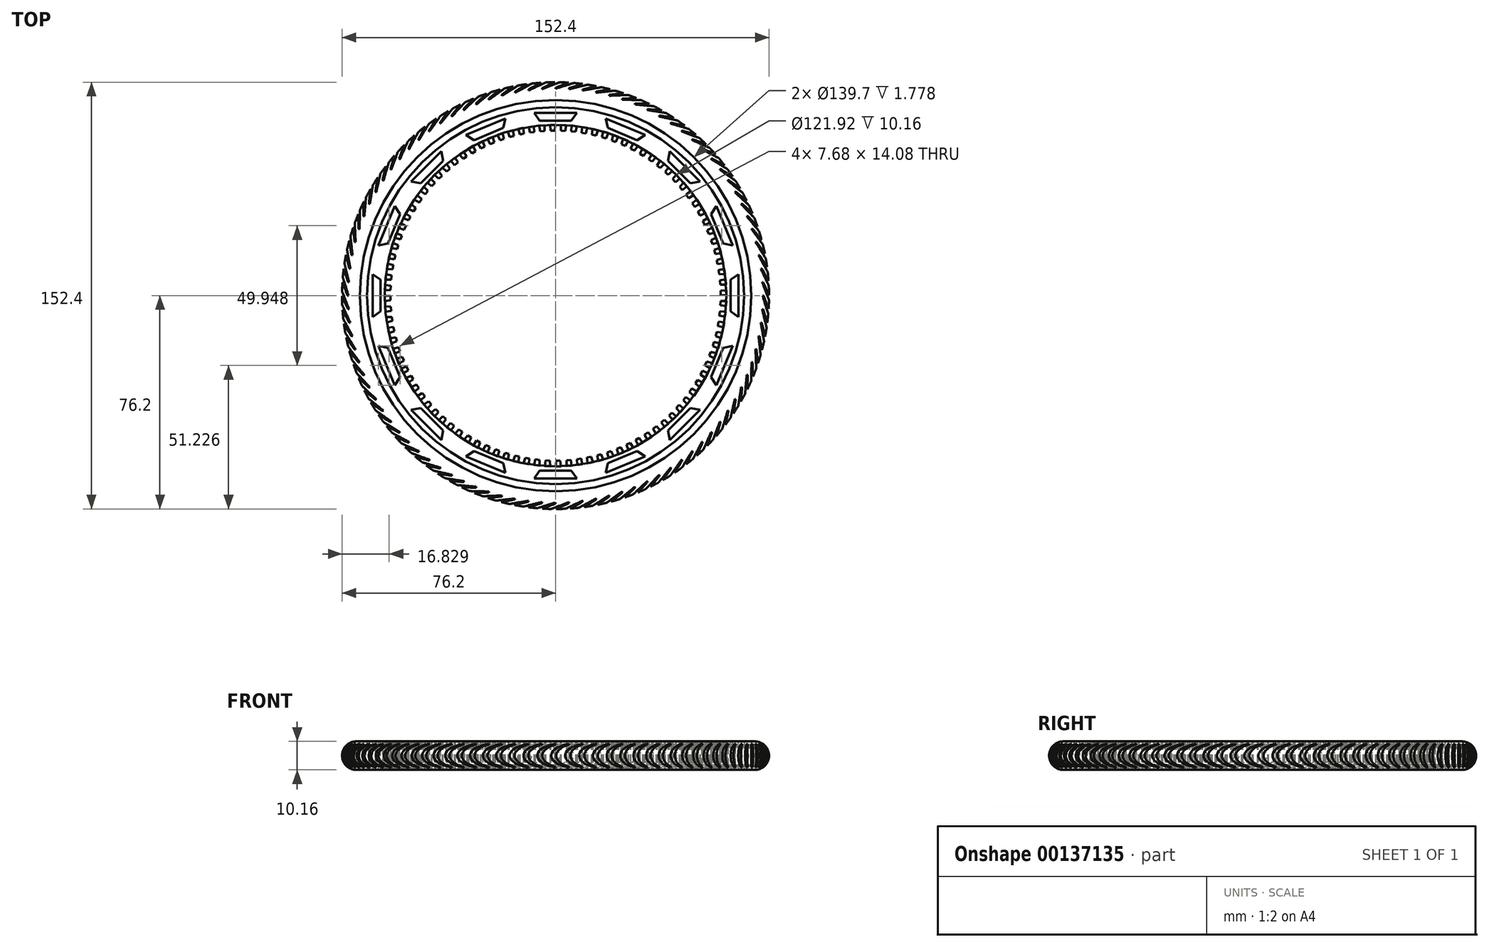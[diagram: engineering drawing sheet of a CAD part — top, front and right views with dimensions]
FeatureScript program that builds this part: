
annotation { "Feature Type Name" : "Feature", "Feature Type Description" : "" }
export const myFeature = defineFeature(function(context is Context, id is Id, definition is map)
    precondition{}
    {
        {
            var Q0;
            Q0=qCreatedBy(makeId("Top.planeOp"),FACE);
            var sketch = newSketch(context, id + "F0", { "sketchPlane" : qUnion([Q0])});
            skCircle(sketch, "E0", {"center": v(0, 0) * mm, "radius": 76.2 * mm});
            skCircle(sketch, "E1", {"center": v(0, 0) * mm, "radius": 60.96 * mm});
            skSolve(sketch);
        }
        {
            var Q0;
            Q0 = qSketchRegion(id + "F0", true);
            extrude(context, id + "F1", {"entities" : qUnion([Q0]), "depth" : 10.16 * mm});
        }
        {
            var Q0;
            Q0=makeQuery(id+"F1.opExtrude","SWEPT_FACE",FACE,{"disambiguationData":[OSD([sQuery(id+"F0.wireOp",EDGE,"E0")])]});
            fillet(context, id + "F2", {"entities" : qUnion([Q0]), "radius" : 5.08 * mm, "tangentPropagation" : true, "allowEdgeOverflow" : false});
        }
        {
            var Q0;
            Q0=qCreatedBy(makeId("Front.planeOp"),FACE);
            var sketch = newSketch(context, id + "F3", { "sketchPlane" : qUnion([Q0])});
            skLineSegment(sketch, "E2", {"start": v(0, 10.16) * mm, "end": v(-69.85, 10.16) * mm, "construction": true});
            skLineSegment(sketch, "E3", {"start": v(-69.85, 10.16) * mm, "end": v(-69.85, 0) * mm, "construction": true});
            skLineSegment(sketch, "E4.bottom", {"start": v(-69.85, 0) * mm, "end": v(-67.31, 0) * mm});
            skLineSegment(sketch, "E4.top", {"start": v(-69.85, 1.78) * mm, "end": v(-67.31, 1.78) * mm});
            skLineSegment(sketch, "E4.left", {"start": v(-69.85, 0) * mm, "end": v(-69.85, 1.78) * mm});
            skLineSegment(sketch, "E4.right", {"start": v(-67.31, 0) * mm, "end": v(-67.31, 1.78) * mm});
            skLineSegment(sketch, "E5.bottom", {"start": v(-69.85, 10.16) * mm, "end": v(-67.31, 10.16) * mm});
            skLineSegment(sketch, "E5.top", {"start": v(-69.85, 8.38) * mm, "end": v(-67.31, 8.38) * mm});
            skLineSegment(sketch, "E5.left", {"start": v(-69.85, 10.16) * mm, "end": v(-69.85, 8.38) * mm});
            skLineSegment(sketch, "E5.right", {"start": v(-67.31, 10.16) * mm, "end": v(-67.31, 8.38) * mm});
            skSolve(sketch);
        }
        {
            var Q0;
            Q0=qCreatedBy(makeId("Front.planeOp"),FACE);
            var sketch = newSketch(context, id + "F4", { "sketchPlane" : qUnion([Q0])});
            skLineSegment(sketch, "E6", {"start": v(0, 100.83) * mm, "end": v(0, -94.42) * mm, "construction": true});
            skSolve(sketch);
        }
        {
            var Q0;
            Q0 = qSketchRegion(id + "F3", true);
            var Q1;
            Q1=sQuery(id+"F4.wireOp",EDGE,"E6");
            revolve(context, id + "F5", {"operationType" : NewBodyOperationType.REMOVE, "entities" : qUnion([Q0]), "axis" : qUnion([Q1]), "revolveType" : RevolveType.FULL, "oppositeDirection" : true});
        }
        {
            var Q0;
            {var subQ0=sQuery(id+"F0.wireOp",EDGE,"E1");Q0=makeQuery(id+"F5.boolean.opBoolean","SPLIT",FACE,{"disambiguationData":[TD([makeQuery(id+"F1.opExtrude","SWEPT_FACE",FACE,{"disambiguationData":[OSD([subQ0])]})])],"derivedFrom":makeQuery(id+"F1.opExtrude","CAP_FACE",FACE,{"disambiguationData":[OSD([sQuery(id+"F0.wireOp",EDGE,"E0"),subQ0])],"isStart":true})});}
            var sketch = newSketch(context, id + "F6", { "sketchPlane" : qUnion([Q0])});
            skLineSegment(sketch, "E7", {"start": v(3.9, 60.84) * mm, "end": v(3.9, 58.8) * mm});
            skLineSegment(sketch, "E8", {"start": v(3.9, 58.8) * mm, "end": v(5.43, 58.68) * mm});
            skLineSegment(sketch, "E9", {"start": v(5.43, 58.68) * mm, "end": v(5.76, 60.69) * mm});
            skLineSegment(sketch, "E10", {"start": v(3.9, 60.84) * mm, "end": v(5.76, 60.69) * mm});
            skLineSegment(sketch, "E11.1.0", {"start": v(0.06, 60.96) * mm, "end": v(0.2, 58.93) * mm});
            skLineSegment(sketch, "E11.1.1", {"start": v(0.06, 60.96) * mm, "end": v(1.94, 60.93) * mm});
            skLineSegment(sketch, "E11.1.2", {"start": v(1.73, 58.9) * mm, "end": v(1.94, 60.93) * mm});
            skLineSegment(sketch, "E11.1.3", {"start": v(0.2, 58.93) * mm, "end": v(1.73, 58.9) * mm});
            skLineSegment(sketch, "E11.2.0", {"start": v(-3.76, 60.84) * mm, "end": v(-3.5, 58.83) * mm});
            skLineSegment(sketch, "E11.2.1", {"start": v(-3.76, 60.84) * mm, "end": v(-1.89, 60.93) * mm});
            skLineSegment(sketch, "E11.2.2", {"start": v(-1.97, 58.9) * mm, "end": v(-1.89, 60.93) * mm});
            skLineSegment(sketch, "E11.2.3", {"start": v(-3.5, 58.83) * mm, "end": v(-1.97, 58.9) * mm});
            skLineSegment(sketch, "E11.3.0", {"start": v(-7.58, 60.49) * mm, "end": v(-7.18, 58.5) * mm});
            skLineSegment(sketch, "E11.3.1", {"start": v(-7.58, 60.49) * mm, "end": v(-5.71, 60.7) * mm});
            skLineSegment(sketch, "E11.3.2", {"start": v(-5.67, 58.66) * mm, "end": v(-5.71, 60.7) * mm});
            skLineSegment(sketch, "E11.3.3", {"start": v(-7.18, 58.5) * mm, "end": v(-5.67, 58.66) * mm});
            skLineSegment(sketch, "E11.4.0", {"start": v(-11.36, 59.9) * mm, "end": v(-10.84, 57.93) * mm});
            skLineSegment(sketch, "E11.4.1", {"start": v(-11.36, 59.9) * mm, "end": v(-9.51, 60.21) * mm});
            skLineSegment(sketch, "E11.4.2", {"start": v(-9.34, 58.19) * mm, "end": v(-9.51, 60.21) * mm});
            skLineSegment(sketch, "E11.4.3", {"start": v(-10.84, 57.93) * mm, "end": v(-9.34, 58.19) * mm});
            skLineSegment(sketch, "E11.5.0", {"start": v(-15.1, 59.06) * mm, "end": v(-14.46, 57.13) * mm});
            skLineSegment(sketch, "E11.5.1", {"start": v(-15.1, 59.06) * mm, "end": v(-13.27, 59.5) * mm});
            skLineSegment(sketch, "E11.5.2", {"start": v(-12.97, 57.49) * mm, "end": v(-13.27, 59.5) * mm});
            skLineSegment(sketch, "E11.5.3", {"start": v(-14.46, 57.13) * mm, "end": v(-12.97, 57.49) * mm});
            skLineSegment(sketch, "E11.6.0", {"start": v(-18.78, 58) * mm, "end": v(-18.01, 56.11) * mm});
            skLineSegment(sketch, "E11.6.1", {"start": v(-18.78, 58) * mm, "end": v(-16.98, 58.55) * mm});
            skLineSegment(sketch, "E11.6.2", {"start": v(-16.56, 56.56) * mm, "end": v(-16.98, 58.55) * mm});
            skLineSegment(sketch, "E11.6.3", {"start": v(-18.01, 56.11) * mm, "end": v(-16.56, 56.56) * mm});
            skLineSegment(sketch, "E11.7.0", {"start": v(-22.38, 56.7) * mm, "end": v(-21.5, 54.87) * mm});
            skLineSegment(sketch, "E11.7.1", {"start": v(-22.38, 56.7) * mm, "end": v(-20.62, 57.37) * mm});
            skLineSegment(sketch, "E11.7.2", {"start": v(-20.08, 55.4) * mm, "end": v(-20.62, 57.37) * mm});
            skLineSegment(sketch, "E11.7.3", {"start": v(-21.5, 54.87) * mm, "end": v(-20.08, 55.4) * mm});
            skLineSegment(sketch, "E11.8.0", {"start": v(-25.9, 55.19) * mm, "end": v(-24.9, 53.41) * mm});
            skLineSegment(sketch, "E11.8.1", {"start": v(-25.9, 55.19) * mm, "end": v(-24.19, 55.96) * mm});
            skLineSegment(sketch, "E11.8.2", {"start": v(-23.52, 54.04) * mm, "end": v(-24.19, 55.96) * mm});
            skLineSegment(sketch, "E11.8.3", {"start": v(-24.9, 53.41) * mm, "end": v(-23.52, 54.04) * mm});
            skLineSegment(sketch, "E11.9.0", {"start": v(-29.31, 53.45) * mm, "end": v(-28.2, 51.74) * mm});
            skLineSegment(sketch, "E11.9.1", {"start": v(-29.31, 53.45) * mm, "end": v(-27.65, 54.33) * mm});
            skLineSegment(sketch, "E11.9.2", {"start": v(-26.86, 52.46) * mm, "end": v(-27.65, 54.33) * mm});
            skLineSegment(sketch, "E11.9.3", {"start": v(-28.2, 51.74) * mm, "end": v(-26.86, 52.46) * mm});
            skLineSegment(sketch, "E11.10.0", {"start": v(-32.61, 51.5) * mm, "end": v(-31.4, 49.87) * mm});
            skLineSegment(sketch, "E11.10.1", {"start": v(-32.61, 51.5) * mm, "end": v(-31, 52.48) * mm});
            skLineSegment(sketch, "E11.10.2", {"start": v(-30.1, 50.67) * mm, "end": v(-31, 52.48) * mm});
            skLineSegment(sketch, "E11.10.3", {"start": v(-31.4, 49.87) * mm, "end": v(-30.1, 50.67) * mm});
            skLineSegment(sketch, "E11.11.0", {"start": v(-35.78, 49.35) * mm, "end": v(-34.47, 47.8) * mm});
            skLineSegment(sketch, "E11.11.1", {"start": v(-35.78, 49.35) * mm, "end": v(-34.24, 50.43) * mm});
            skLineSegment(sketch, "E11.11.2", {"start": v(-33.23, 48.67) * mm, "end": v(-34.24, 50.43) * mm});
            skLineSegment(sketch, "E11.11.3", {"start": v(-34.47, 47.8) * mm, "end": v(-33.23, 48.67) * mm});
            skLineSegment(sketch, "E11.12.0", {"start": v(-38.8, 47.01) * mm, "end": v(-37.4, 45.54) * mm});
            skLineSegment(sketch, "E11.12.1", {"start": v(-38.8, 47.01) * mm, "end": v(-37.34, 48.18) * mm});
            skLineSegment(sketch, "E11.12.2", {"start": v(-36.22, 46.5) * mm, "end": v(-37.34, 48.18) * mm});
            skLineSegment(sketch, "E11.12.3", {"start": v(-37.4, 45.54) * mm, "end": v(-36.22, 46.5) * mm});
            skLineSegment(sketch, "E11.13.0", {"start": v(-41.68, 44.48) * mm, "end": v(-40.2, 43.1) * mm});
            skLineSegment(sketch, "E11.13.1", {"start": v(-41.68, 44.48) * mm, "end": v(-40.3, 45.74) * mm});
            skLineSegment(sketch, "E11.13.2", {"start": v(-39.06, 44.13) * mm, "end": v(-40.3, 45.74) * mm});
            skLineSegment(sketch, "E11.13.3", {"start": v(-40.2, 43.1) * mm, "end": v(-39.06, 44.13) * mm});
            skLineSegment(sketch, "E11.14.0", {"start": v(-44.4, 41.78) * mm, "end": v(-42.82, 40.5) * mm});
            skLineSegment(sketch, "E11.14.1", {"start": v(-44.4, 41.78) * mm, "end": v(-43.09, 43.12) * mm});
            skLineSegment(sketch, "E11.14.2", {"start": v(-41.76, 41.59) * mm, "end": v(-43.09, 43.12) * mm});
            skLineSegment(sketch, "E11.14.3", {"start": v(-42.82, 40.5) * mm, "end": v(-41.76, 41.59) * mm});
            skLineSegment(sketch, "E11.15.0", {"start": v(-46.93, 38.9) * mm, "end": v(-45.28, 37.72) * mm});
            skLineSegment(sketch, "E11.15.1", {"start": v(-46.93, 38.9) * mm, "end": v(-45.7, 40.33) * mm});
            skLineSegment(sketch, "E11.15.2", {"start": v(-44.29, 38.88) * mm, "end": v(-45.7, 40.33) * mm});
            skLineSegment(sketch, "E11.15.3", {"start": v(-45.28, 37.72) * mm, "end": v(-44.29, 38.88) * mm});
            skLineSegment(sketch, "E11.16.0", {"start": v(-49.28, 35.88) * mm, "end": v(-47.56, 34.8) * mm});
            skLineSegment(sketch, "E11.16.1", {"start": v(-49.28, 35.88) * mm, "end": v(-48.15, 37.38) * mm});
            skLineSegment(sketch, "E11.16.2", {"start": v(-46.64, 36.03) * mm, "end": v(-48.15, 37.38) * mm});
            skLineSegment(sketch, "E11.16.3", {"start": v(-47.56, 34.8) * mm, "end": v(-46.64, 36.03) * mm});
            skLineSegment(sketch, "E11.17.0", {"start": v(-51.44, 32.72) * mm, "end": v(-49.65, 31.75) * mm});
            skLineSegment(sketch, "E11.17.1", {"start": v(-51.44, 32.72) * mm, "end": v(-50.4, 34.29) * mm});
            skLineSegment(sketch, "E11.17.2", {"start": v(-48.81, 33.03) * mm, "end": v(-50.4, 34.29) * mm});
            skLineSegment(sketch, "E11.17.3", {"start": v(-49.65, 31.75) * mm, "end": v(-48.81, 33.03) * mm});
            skLineSegment(sketch, "E11.18.0", {"start": v(-53.39, 29.42) * mm, "end": v(-51.54, 28.57) * mm});
            skLineSegment(sketch, "E11.18.1", {"start": v(-53.39, 29.42) * mm, "end": v(-52.46, 31.05) * mm});
            skLineSegment(sketch, "E11.18.2", {"start": v(-50.79, 29.9) * mm, "end": v(-52.46, 31.05) * mm});
            skLineSegment(sketch, "E11.18.3", {"start": v(-51.54, 28.57) * mm, "end": v(-50.79, 29.9) * mm});
            skLineSegment(sketch, "E11.19.0", {"start": v(-55.13, 26.01) * mm, "end": v(-53.24, 25.28) * mm});
            skLineSegment(sketch, "E11.19.1", {"start": v(-55.13, 26.01) * mm, "end": v(-54.3, 27.7) * mm});
            skLineSegment(sketch, "E11.19.2", {"start": v(-52.56, 26.65) * mm, "end": v(-54.3, 27.7) * mm});
            skLineSegment(sketch, "E11.19.3", {"start": v(-53.24, 25.28) * mm, "end": v(-52.56, 26.65) * mm});
            skLineSegment(sketch, "E11.20.0", {"start": v(-56.66, 22.5) * mm, "end": v(-54.72, 21.89) * mm});
            skLineSegment(sketch, "E11.20.1", {"start": v(-56.66, 22.5) * mm, "end": v(-55.94, 24.23) * mm});
            skLineSegment(sketch, "E11.20.2", {"start": v(-54.13, 23.3) * mm, "end": v(-55.94, 24.23) * mm});
            skLineSegment(sketch, "E11.20.3", {"start": v(-54.72, 21.89) * mm, "end": v(-54.13, 23.3) * mm});
            skLineSegment(sketch, "E11.21.0", {"start": v(-57.96, 18.9) * mm, "end": v(-55.98, 18.4) * mm});
            skLineSegment(sketch, "E11.21.1", {"start": v(-57.96, 18.9) * mm, "end": v(-57.35, 20.67) * mm});
            skLineSegment(sketch, "E11.21.2", {"start": v(-55.5, 19.85) * mm, "end": v(-57.35, 20.67) * mm});
            skLineSegment(sketch, "E11.21.3", {"start": v(-55.98, 18.4) * mm, "end": v(-55.5, 19.85) * mm});
            skLineSegment(sketch, "E11.22.0", {"start": v(-59.03, 15.22) * mm, "end": v(-57.03, 14.86) * mm});
            skLineSegment(sketch, "E11.22.1", {"start": v(-59.03, 15.22) * mm, "end": v(-58.53, 17.03) * mm});
            skLineSegment(sketch, "E11.22.2", {"start": v(-56.63, 16.33) * mm, "end": v(-58.53, 17.03) * mm});
            skLineSegment(sketch, "E11.22.3", {"start": v(-57.03, 14.86) * mm, "end": v(-56.63, 16.33) * mm});
            skLineSegment(sketch, "E11.23.0", {"start": v(-59.87, 11.48) * mm, "end": v(-57.85, 11.25) * mm});
            skLineSegment(sketch, "E11.23.1", {"start": v(-59.87, 11.48) * mm, "end": v(-59.49, 13.32) * mm});
            skLineSegment(sketch, "E11.23.2", {"start": v(-57.54, 12.74) * mm, "end": v(-59.49, 13.32) * mm});
            skLineSegment(sketch, "E11.23.3", {"start": v(-57.85, 11.25) * mm, "end": v(-57.54, 12.74) * mm});
            skLineSegment(sketch, "E11.24.0", {"start": v(-60.47, 7.7) * mm, "end": v(-58.44, 7.6) * mm});
            skLineSegment(sketch, "E11.24.1", {"start": v(-60.47, 7.7) * mm, "end": v(-60.2, 9.56) * mm});
            skLineSegment(sketch, "E11.24.2", {"start": v(-58.23, 9.1) * mm, "end": v(-60.2, 9.56) * mm});
            skLineSegment(sketch, "E11.24.3", {"start": v(-58.44, 7.6) * mm, "end": v(-58.23, 9.1) * mm});
            skLineSegment(sketch, "E11.25.0", {"start": v(-60.84, 3.9) * mm, "end": v(-58.8, 3.9) * mm});
            skLineSegment(sketch, "E11.25.1", {"start": v(-60.84, 3.9) * mm, "end": v(-60.69, 5.76) * mm});
            skLineSegment(sketch, "E11.25.2", {"start": v(-58.68, 5.43) * mm, "end": v(-60.69, 5.76) * mm});
            skLineSegment(sketch, "E11.25.3", {"start": v(-58.8, 3.9) * mm, "end": v(-58.68, 5.43) * mm});
            skLineSegment(sketch, "E11.26.0", {"start": v(-60.96, 0.06) * mm, "end": v(-58.93, 0.2) * mm});
            skLineSegment(sketch, "E11.26.1", {"start": v(-60.96, 0.06) * mm, "end": v(-60.93, 1.94) * mm});
            skLineSegment(sketch, "E11.26.2", {"start": v(-58.9, 1.73) * mm, "end": v(-60.93, 1.94) * mm});
            skLineSegment(sketch, "E11.26.3", {"start": v(-58.93, 0.2) * mm, "end": v(-58.9, 1.73) * mm});
            skLineSegment(sketch, "E11.27.0", {"start": v(-60.84, -3.76) * mm, "end": v(-58.83, -3.5) * mm});
            skLineSegment(sketch, "E11.27.1", {"start": v(-60.84, -3.76) * mm, "end": v(-60.93, -1.89) * mm});
            skLineSegment(sketch, "E11.27.2", {"start": v(-58.9, -1.97) * mm, "end": v(-60.93, -1.89) * mm});
            skLineSegment(sketch, "E11.27.3", {"start": v(-58.83, -3.5) * mm, "end": v(-58.9, -1.97) * mm});
            skLineSegment(sketch, "E11.28.0", {"start": v(-60.49, -7.58) * mm, "end": v(-58.5, -7.18) * mm});
            skLineSegment(sketch, "E11.28.1", {"start": v(-60.49, -7.58) * mm, "end": v(-60.7, -5.71) * mm});
            skLineSegment(sketch, "E11.28.2", {"start": v(-58.66, -5.67) * mm, "end": v(-60.7, -5.71) * mm});
            skLineSegment(sketch, "E11.28.3", {"start": v(-58.5, -7.18) * mm, "end": v(-58.66, -5.67) * mm});
            skLineSegment(sketch, "E11.29.0", {"start": v(-59.9, -11.36) * mm, "end": v(-57.93, -10.84) * mm});
            skLineSegment(sketch, "E11.29.1", {"start": v(-59.9, -11.36) * mm, "end": v(-60.21, -9.51) * mm});
            skLineSegment(sketch, "E11.29.2", {"start": v(-58.19, -9.34) * mm, "end": v(-60.21, -9.51) * mm});
            skLineSegment(sketch, "E11.29.3", {"start": v(-57.93, -10.84) * mm, "end": v(-58.19, -9.34) * mm});
            skLineSegment(sketch, "E11.30.0", {"start": v(-59.06, -15.1) * mm, "end": v(-57.13, -14.46) * mm});
            skLineSegment(sketch, "E11.30.1", {"start": v(-59.06, -15.1) * mm, "end": v(-59.5, -13.27) * mm});
            skLineSegment(sketch, "E11.30.2", {"start": v(-57.49, -12.97) * mm, "end": v(-59.5, -13.27) * mm});
            skLineSegment(sketch, "E11.30.3", {"start": v(-57.13, -14.46) * mm, "end": v(-57.49, -12.97) * mm});
            skLineSegment(sketch, "E11.31.0", {"start": v(-58, -18.78) * mm, "end": v(-56.11, -18.01) * mm});
            skLineSegment(sketch, "E11.31.1", {"start": v(-58, -18.78) * mm, "end": v(-58.55, -16.98) * mm});
            skLineSegment(sketch, "E11.31.2", {"start": v(-56.56, -16.56) * mm, "end": v(-58.55, -16.98) * mm});
            skLineSegment(sketch, "E11.31.3", {"start": v(-56.11, -18.01) * mm, "end": v(-56.56, -16.56) * mm});
            skLineSegment(sketch, "E11.32.0", {"start": v(-56.7, -22.38) * mm, "end": v(-54.87, -21.5) * mm});
            skLineSegment(sketch, "E11.32.1", {"start": v(-56.7, -22.38) * mm, "end": v(-57.37, -20.62) * mm});
            skLineSegment(sketch, "E11.32.2", {"start": v(-55.4, -20.08) * mm, "end": v(-57.37, -20.62) * mm});
            skLineSegment(sketch, "E11.32.3", {"start": v(-54.87, -21.5) * mm, "end": v(-55.4, -20.08) * mm});
            skLineSegment(sketch, "E11.33.0", {"start": v(-55.19, -25.9) * mm, "end": v(-53.41, -24.9) * mm});
            skLineSegment(sketch, "E11.33.1", {"start": v(-55.19, -25.9) * mm, "end": v(-55.96, -24.19) * mm});
            skLineSegment(sketch, "E11.33.2", {"start": v(-54.04, -23.52) * mm, "end": v(-55.96, -24.19) * mm});
            skLineSegment(sketch, "E11.33.3", {"start": v(-53.41, -24.9) * mm, "end": v(-54.04, -23.52) * mm});
            skLineSegment(sketch, "E11.34.0", {"start": v(-53.45, -29.31) * mm, "end": v(-51.74, -28.2) * mm});
            skLineSegment(sketch, "E11.34.1", {"start": v(-53.45, -29.31) * mm, "end": v(-54.33, -27.65) * mm});
            skLineSegment(sketch, "E11.34.2", {"start": v(-52.46, -26.86) * mm, "end": v(-54.33, -27.65) * mm});
            skLineSegment(sketch, "E11.34.3", {"start": v(-51.74, -28.2) * mm, "end": v(-52.46, -26.86) * mm});
            skLineSegment(sketch, "E11.35.0", {"start": v(-51.5, -32.61) * mm, "end": v(-49.87, -31.4) * mm});
            skLineSegment(sketch, "E11.35.1", {"start": v(-51.5, -32.61) * mm, "end": v(-52.48, -31) * mm});
            skLineSegment(sketch, "E11.35.2", {"start": v(-50.67, -30.1) * mm, "end": v(-52.48, -31) * mm});
            skLineSegment(sketch, "E11.35.3", {"start": v(-49.87, -31.4) * mm, "end": v(-50.67, -30.1) * mm});
            skLineSegment(sketch, "E11.36.0", {"start": v(-49.35, -35.78) * mm, "end": v(-47.8, -34.47) * mm});
            skLineSegment(sketch, "E11.36.1", {"start": v(-49.35, -35.78) * mm, "end": v(-50.43, -34.24) * mm});
            skLineSegment(sketch, "E11.36.2", {"start": v(-48.67, -33.23) * mm, "end": v(-50.43, -34.24) * mm});
            skLineSegment(sketch, "E11.36.3", {"start": v(-47.8, -34.47) * mm, "end": v(-48.67, -33.23) * mm});
            skLineSegment(sketch, "E11.37.0", {"start": v(-47.01, -38.8) * mm, "end": v(-45.54, -37.4) * mm});
            skLineSegment(sketch, "E11.37.1", {"start": v(-47.01, -38.8) * mm, "end": v(-48.18, -37.34) * mm});
            skLineSegment(sketch, "E11.37.2", {"start": v(-46.5, -36.22) * mm, "end": v(-48.18, -37.34) * mm});
            skLineSegment(sketch, "E11.37.3", {"start": v(-45.54, -37.4) * mm, "end": v(-46.5, -36.22) * mm});
            skLineSegment(sketch, "E11.38.0", {"start": v(-44.48, -41.68) * mm, "end": v(-43.1, -40.2) * mm});
            skLineSegment(sketch, "E11.38.1", {"start": v(-44.48, -41.68) * mm, "end": v(-45.74, -40.3) * mm});
            skLineSegment(sketch, "E11.38.2", {"start": v(-44.13, -39.06) * mm, "end": v(-45.74, -40.3) * mm});
            skLineSegment(sketch, "E11.38.3", {"start": v(-43.1, -40.2) * mm, "end": v(-44.13, -39.06) * mm});
            skLineSegment(sketch, "E11.39.0", {"start": v(-41.78, -44.4) * mm, "end": v(-40.5, -42.82) * mm});
            skLineSegment(sketch, "E11.39.1", {"start": v(-41.78, -44.4) * mm, "end": v(-43.12, -43.09) * mm});
            skLineSegment(sketch, "E11.39.2", {"start": v(-41.59, -41.76) * mm, "end": v(-43.12, -43.09) * mm});
            skLineSegment(sketch, "E11.39.3", {"start": v(-40.5, -42.82) * mm, "end": v(-41.59, -41.76) * mm});
            skLineSegment(sketch, "E11.40.0", {"start": v(-38.9, -46.93) * mm, "end": v(-37.72, -45.28) * mm});
            skLineSegment(sketch, "E11.40.1", {"start": v(-38.9, -46.93) * mm, "end": v(-40.33, -45.7) * mm});
            skLineSegment(sketch, "E11.40.2", {"start": v(-38.88, -44.29) * mm, "end": v(-40.33, -45.7) * mm});
            skLineSegment(sketch, "E11.40.3", {"start": v(-37.72, -45.28) * mm, "end": v(-38.88, -44.29) * mm});
            skLineSegment(sketch, "E11.41.0", {"start": v(-35.88, -49.28) * mm, "end": v(-34.8, -47.56) * mm});
            skLineSegment(sketch, "E11.41.1", {"start": v(-35.88, -49.28) * mm, "end": v(-37.38, -48.15) * mm});
            skLineSegment(sketch, "E11.41.2", {"start": v(-36.03, -46.64) * mm, "end": v(-37.38, -48.15) * mm});
            skLineSegment(sketch, "E11.41.3", {"start": v(-34.8, -47.56) * mm, "end": v(-36.03, -46.64) * mm});
            skLineSegment(sketch, "E11.42.0", {"start": v(-32.72, -51.44) * mm, "end": v(-31.75, -49.65) * mm});
            skLineSegment(sketch, "E11.42.1", {"start": v(-32.72, -51.44) * mm, "end": v(-34.29, -50.4) * mm});
            skLineSegment(sketch, "E11.42.2", {"start": v(-33.03, -48.81) * mm, "end": v(-34.29, -50.4) * mm});
            skLineSegment(sketch, "E11.42.3", {"start": v(-31.75, -49.65) * mm, "end": v(-33.03, -48.81) * mm});
            skLineSegment(sketch, "E11.43.0", {"start": v(-29.42, -53.39) * mm, "end": v(-28.57, -51.54) * mm});
            skLineSegment(sketch, "E11.43.1", {"start": v(-29.42, -53.39) * mm, "end": v(-31.05, -52.46) * mm});
            skLineSegment(sketch, "E11.43.2", {"start": v(-29.9, -50.79) * mm, "end": v(-31.05, -52.46) * mm});
            skLineSegment(sketch, "E11.43.3", {"start": v(-28.57, -51.54) * mm, "end": v(-29.9, -50.79) * mm});
            skLineSegment(sketch, "E11.44.0", {"start": v(-26.01, -55.13) * mm, "end": v(-25.28, -53.24) * mm});
            skLineSegment(sketch, "E11.44.1", {"start": v(-26.01, -55.13) * mm, "end": v(-27.7, -54.3) * mm});
            skLineSegment(sketch, "E11.44.2", {"start": v(-26.65, -52.56) * mm, "end": v(-27.7, -54.3) * mm});
            skLineSegment(sketch, "E11.44.3", {"start": v(-25.28, -53.24) * mm, "end": v(-26.65, -52.56) * mm});
            skLineSegment(sketch, "E11.45.0", {"start": v(-22.5, -56.66) * mm, "end": v(-21.89, -54.72) * mm});
            skLineSegment(sketch, "E11.45.1", {"start": v(-22.5, -56.66) * mm, "end": v(-24.23, -55.94) * mm});
            skLineSegment(sketch, "E11.45.2", {"start": v(-23.3, -54.13) * mm, "end": v(-24.23, -55.94) * mm});
            skLineSegment(sketch, "E11.45.3", {"start": v(-21.89, -54.72) * mm, "end": v(-23.3, -54.13) * mm});
            skLineSegment(sketch, "E11.46.0", {"start": v(-18.9, -57.96) * mm, "end": v(-18.4, -55.98) * mm});
            skLineSegment(sketch, "E11.46.1", {"start": v(-18.9, -57.96) * mm, "end": v(-20.67, -57.35) * mm});
            skLineSegment(sketch, "E11.46.2", {"start": v(-19.85, -55.5) * mm, "end": v(-20.67, -57.35) * mm});
            skLineSegment(sketch, "E11.46.3", {"start": v(-18.4, -55.98) * mm, "end": v(-19.85, -55.5) * mm});
            skLineSegment(sketch, "E11.47.0", {"start": v(-15.22, -59.03) * mm, "end": v(-14.86, -57.03) * mm});
            skLineSegment(sketch, "E11.47.1", {"start": v(-15.22, -59.03) * mm, "end": v(-17.03, -58.53) * mm});
            skLineSegment(sketch, "E11.47.2", {"start": v(-16.33, -56.63) * mm, "end": v(-17.03, -58.53) * mm});
            skLineSegment(sketch, "E11.47.3", {"start": v(-14.86, -57.03) * mm, "end": v(-16.33, -56.63) * mm});
            skLineSegment(sketch, "E11.48.0", {"start": v(-11.48, -59.87) * mm, "end": v(-11.25, -57.85) * mm});
            skLineSegment(sketch, "E11.48.1", {"start": v(-11.48, -59.87) * mm, "end": v(-13.32, -59.49) * mm});
            skLineSegment(sketch, "E11.48.2", {"start": v(-12.74, -57.54) * mm, "end": v(-13.32, -59.49) * mm});
            skLineSegment(sketch, "E11.48.3", {"start": v(-11.25, -57.85) * mm, "end": v(-12.74, -57.54) * mm});
            skLineSegment(sketch, "E11.49.0", {"start": v(-7.7, -60.47) * mm, "end": v(-7.6, -58.44) * mm});
            skLineSegment(sketch, "E11.49.1", {"start": v(-7.7, -60.47) * mm, "end": v(-9.56, -60.2) * mm});
            skLineSegment(sketch, "E11.49.2", {"start": v(-9.1, -58.23) * mm, "end": v(-9.56, -60.2) * mm});
            skLineSegment(sketch, "E11.49.3", {"start": v(-7.6, -58.44) * mm, "end": v(-9.1, -58.23) * mm});
            skLineSegment(sketch, "E11.50.0", {"start": v(-3.9, -60.84) * mm, "end": v(-3.9, -58.8) * mm});
            skLineSegment(sketch, "E11.50.1", {"start": v(-3.9, -60.84) * mm, "end": v(-5.76, -60.69) * mm});
            skLineSegment(sketch, "E11.50.2", {"start": v(-5.43, -58.68) * mm, "end": v(-5.76, -60.69) * mm});
            skLineSegment(sketch, "E11.50.3", {"start": v(-3.9, -58.8) * mm, "end": v(-5.43, -58.68) * mm});
            skLineSegment(sketch, "E11.51.0", {"start": v(-0.06, -60.96) * mm, "end": v(-0.2, -58.93) * mm});
            skLineSegment(sketch, "E11.51.1", {"start": v(-0.06, -60.96) * mm, "end": v(-1.94, -60.93) * mm});
            skLineSegment(sketch, "E11.51.2", {"start": v(-1.73, -58.9) * mm, "end": v(-1.94, -60.93) * mm});
            skLineSegment(sketch, "E11.51.3", {"start": v(-0.2, -58.93) * mm, "end": v(-1.73, -58.9) * mm});
            skLineSegment(sketch, "E11.52.0", {"start": v(3.76, -60.84) * mm, "end": v(3.5, -58.83) * mm});
            skLineSegment(sketch, "E11.52.1", {"start": v(3.76, -60.84) * mm, "end": v(1.89, -60.93) * mm});
            skLineSegment(sketch, "E11.52.2", {"start": v(1.97, -58.9) * mm, "end": v(1.89, -60.93) * mm});
            skLineSegment(sketch, "E11.52.3", {"start": v(3.5, -58.83) * mm, "end": v(1.97, -58.9) * mm});
            skLineSegment(sketch, "E11.53.0", {"start": v(7.58, -60.49) * mm, "end": v(7.18, -58.5) * mm});
            skLineSegment(sketch, "E11.53.1", {"start": v(7.58, -60.49) * mm, "end": v(5.71, -60.7) * mm});
            skLineSegment(sketch, "E11.53.2", {"start": v(5.67, -58.66) * mm, "end": v(5.71, -60.7) * mm});
            skLineSegment(sketch, "E11.53.3", {"start": v(7.18, -58.5) * mm, "end": v(5.67, -58.66) * mm});
            skLineSegment(sketch, "E11.54.0", {"start": v(11.36, -59.9) * mm, "end": v(10.84, -57.93) * mm});
            skLineSegment(sketch, "E11.54.1", {"start": v(11.36, -59.9) * mm, "end": v(9.51, -60.21) * mm});
            skLineSegment(sketch, "E11.54.2", {"start": v(9.34, -58.19) * mm, "end": v(9.51, -60.21) * mm});
            skLineSegment(sketch, "E11.54.3", {"start": v(10.84, -57.93) * mm, "end": v(9.34, -58.19) * mm});
            skLineSegment(sketch, "E11.55.0", {"start": v(15.1, -59.06) * mm, "end": v(14.46, -57.13) * mm});
            skLineSegment(sketch, "E11.55.1", {"start": v(15.1, -59.06) * mm, "end": v(13.27, -59.5) * mm});
            skLineSegment(sketch, "E11.55.2", {"start": v(12.97, -57.49) * mm, "end": v(13.27, -59.5) * mm});
            skLineSegment(sketch, "E11.55.3", {"start": v(14.46, -57.13) * mm, "end": v(12.97, -57.49) * mm});
            skLineSegment(sketch, "E11.56.0", {"start": v(18.78, -58) * mm, "end": v(18.01, -56.11) * mm});
            skLineSegment(sketch, "E11.56.1", {"start": v(18.78, -58) * mm, "end": v(16.98, -58.55) * mm});
            skLineSegment(sketch, "E11.56.2", {"start": v(16.56, -56.56) * mm, "end": v(16.98, -58.55) * mm});
            skLineSegment(sketch, "E11.56.3", {"start": v(18.01, -56.11) * mm, "end": v(16.56, -56.56) * mm});
            skLineSegment(sketch, "E11.57.0", {"start": v(22.38, -56.7) * mm, "end": v(21.5, -54.87) * mm});
            skLineSegment(sketch, "E11.57.1", {"start": v(22.38, -56.7) * mm, "end": v(20.62, -57.37) * mm});
            skLineSegment(sketch, "E11.57.2", {"start": v(20.08, -55.4) * mm, "end": v(20.62, -57.37) * mm});
            skLineSegment(sketch, "E11.57.3", {"start": v(21.5, -54.87) * mm, "end": v(20.08, -55.4) * mm});
            skLineSegment(sketch, "E11.58.0", {"start": v(25.9, -55.19) * mm, "end": v(24.9, -53.41) * mm});
            skLineSegment(sketch, "E11.58.1", {"start": v(25.9, -55.19) * mm, "end": v(24.19, -55.96) * mm});
            skLineSegment(sketch, "E11.58.2", {"start": v(23.52, -54.04) * mm, "end": v(24.19, -55.96) * mm});
            skLineSegment(sketch, "E11.58.3", {"start": v(24.9, -53.41) * mm, "end": v(23.52, -54.04) * mm});
            skLineSegment(sketch, "E11.59.0", {"start": v(29.31, -53.45) * mm, "end": v(28.2, -51.74) * mm});
            skLineSegment(sketch, "E11.59.1", {"start": v(29.31, -53.45) * mm, "end": v(27.65, -54.33) * mm});
            skLineSegment(sketch, "E11.59.2", {"start": v(26.86, -52.46) * mm, "end": v(27.65, -54.33) * mm});
            skLineSegment(sketch, "E11.59.3", {"start": v(28.2, -51.74) * mm, "end": v(26.86, -52.46) * mm});
            skLineSegment(sketch, "E11.60.0", {"start": v(32.61, -51.5) * mm, "end": v(31.4, -49.87) * mm});
            skLineSegment(sketch, "E11.60.1", {"start": v(32.61, -51.5) * mm, "end": v(31, -52.48) * mm});
            skLineSegment(sketch, "E11.60.2", {"start": v(30.1, -50.67) * mm, "end": v(31, -52.48) * mm});
            skLineSegment(sketch, "E11.60.3", {"start": v(31.4, -49.87) * mm, "end": v(30.1, -50.67) * mm});
            skLineSegment(sketch, "E11.61.0", {"start": v(35.78, -49.35) * mm, "end": v(34.47, -47.8) * mm});
            skLineSegment(sketch, "E11.61.1", {"start": v(35.78, -49.35) * mm, "end": v(34.24, -50.43) * mm});
            skLineSegment(sketch, "E11.61.2", {"start": v(33.23, -48.67) * mm, "end": v(34.24, -50.43) * mm});
            skLineSegment(sketch, "E11.61.3", {"start": v(34.47, -47.8) * mm, "end": v(33.23, -48.67) * mm});
            skLineSegment(sketch, "E11.62.0", {"start": v(38.8, -47.01) * mm, "end": v(37.4, -45.54) * mm});
            skLineSegment(sketch, "E11.62.1", {"start": v(38.8, -47.01) * mm, "end": v(37.34, -48.18) * mm});
            skLineSegment(sketch, "E11.62.2", {"start": v(36.22, -46.5) * mm, "end": v(37.34, -48.18) * mm});
            skLineSegment(sketch, "E11.62.3", {"start": v(37.4, -45.54) * mm, "end": v(36.22, -46.5) * mm});
            skLineSegment(sketch, "E11.63.0", {"start": v(41.68, -44.48) * mm, "end": v(40.2, -43.1) * mm});
            skLineSegment(sketch, "E11.63.1", {"start": v(41.68, -44.48) * mm, "end": v(40.3, -45.74) * mm});
            skLineSegment(sketch, "E11.63.2", {"start": v(39.06, -44.13) * mm, "end": v(40.3, -45.74) * mm});
            skLineSegment(sketch, "E11.63.3", {"start": v(40.2, -43.1) * mm, "end": v(39.06, -44.13) * mm});
            skLineSegment(sketch, "E11.64.0", {"start": v(44.4, -41.78) * mm, "end": v(42.82, -40.5) * mm});
            skLineSegment(sketch, "E11.64.1", {"start": v(44.4, -41.78) * mm, "end": v(43.09, -43.12) * mm});
            skLineSegment(sketch, "E11.64.2", {"start": v(41.76, -41.59) * mm, "end": v(43.09, -43.12) * mm});
            skLineSegment(sketch, "E11.64.3", {"start": v(42.82, -40.5) * mm, "end": v(41.76, -41.59) * mm});
            skLineSegment(sketch, "E11.65.0", {"start": v(46.93, -38.9) * mm, "end": v(45.28, -37.72) * mm});
            skLineSegment(sketch, "E11.65.1", {"start": v(46.93, -38.9) * mm, "end": v(45.7, -40.33) * mm});
            skLineSegment(sketch, "E11.65.2", {"start": v(44.29, -38.88) * mm, "end": v(45.7, -40.33) * mm});
            skLineSegment(sketch, "E11.65.3", {"start": v(45.28, -37.72) * mm, "end": v(44.29, -38.88) * mm});
            skLineSegment(sketch, "E11.66.0", {"start": v(49.28, -35.88) * mm, "end": v(47.56, -34.8) * mm});
            skLineSegment(sketch, "E11.66.1", {"start": v(49.28, -35.88) * mm, "end": v(48.15, -37.38) * mm});
            skLineSegment(sketch, "E11.66.2", {"start": v(46.64, -36.03) * mm, "end": v(48.15, -37.38) * mm});
            skLineSegment(sketch, "E11.66.3", {"start": v(47.56, -34.8) * mm, "end": v(46.64, -36.03) * mm});
            skLineSegment(sketch, "E11.67.0", {"start": v(51.44, -32.72) * mm, "end": v(49.65, -31.75) * mm});
            skLineSegment(sketch, "E11.67.1", {"start": v(51.44, -32.72) * mm, "end": v(50.4, -34.29) * mm});
            skLineSegment(sketch, "E11.67.2", {"start": v(48.81, -33.03) * mm, "end": v(50.4, -34.29) * mm});
            skLineSegment(sketch, "E11.67.3", {"start": v(49.65, -31.75) * mm, "end": v(48.81, -33.03) * mm});
            skLineSegment(sketch, "E11.68.0", {"start": v(53.39, -29.42) * mm, "end": v(51.54, -28.57) * mm});
            skLineSegment(sketch, "E11.68.1", {"start": v(53.39, -29.42) * mm, "end": v(52.46, -31.05) * mm});
            skLineSegment(sketch, "E11.68.2", {"start": v(50.79, -29.9) * mm, "end": v(52.46, -31.05) * mm});
            skLineSegment(sketch, "E11.68.3", {"start": v(51.54, -28.57) * mm, "end": v(50.79, -29.9) * mm});
            skLineSegment(sketch, "E11.69.0", {"start": v(55.13, -26.01) * mm, "end": v(53.24, -25.28) * mm});
            skLineSegment(sketch, "E11.69.1", {"start": v(55.13, -26.01) * mm, "end": v(54.3, -27.7) * mm});
            skLineSegment(sketch, "E11.69.2", {"start": v(52.56, -26.65) * mm, "end": v(54.3, -27.7) * mm});
            skLineSegment(sketch, "E11.69.3", {"start": v(53.24, -25.28) * mm, "end": v(52.56, -26.65) * mm});
            skLineSegment(sketch, "E11.70.0", {"start": v(56.66, -22.5) * mm, "end": v(54.72, -21.89) * mm});
            skLineSegment(sketch, "E11.70.1", {"start": v(56.66, -22.5) * mm, "end": v(55.94, -24.23) * mm});
            skLineSegment(sketch, "E11.70.2", {"start": v(54.13, -23.3) * mm, "end": v(55.94, -24.23) * mm});
            skLineSegment(sketch, "E11.70.3", {"start": v(54.72, -21.89) * mm, "end": v(54.13, -23.3) * mm});
            skLineSegment(sketch, "E11.71.0", {"start": v(57.96, -18.9) * mm, "end": v(55.98, -18.4) * mm});
            skLineSegment(sketch, "E11.71.1", {"start": v(57.96, -18.9) * mm, "end": v(57.35, -20.67) * mm});
            skLineSegment(sketch, "E11.71.2", {"start": v(55.5, -19.85) * mm, "end": v(57.35, -20.67) * mm});
            skLineSegment(sketch, "E11.71.3", {"start": v(55.98, -18.4) * mm, "end": v(55.5, -19.85) * mm});
            skLineSegment(sketch, "E11.72.0", {"start": v(59.03, -15.22) * mm, "end": v(57.03, -14.86) * mm});
            skLineSegment(sketch, "E11.72.1", {"start": v(59.03, -15.22) * mm, "end": v(58.53, -17.03) * mm});
            skLineSegment(sketch, "E11.72.2", {"start": v(56.63, -16.33) * mm, "end": v(58.53, -17.03) * mm});
            skLineSegment(sketch, "E11.72.3", {"start": v(57.03, -14.86) * mm, "end": v(56.63, -16.33) * mm});
            skLineSegment(sketch, "E11.73.0", {"start": v(59.87, -11.48) * mm, "end": v(57.85, -11.25) * mm});
            skLineSegment(sketch, "E11.73.1", {"start": v(59.87, -11.48) * mm, "end": v(59.49, -13.32) * mm});
            skLineSegment(sketch, "E11.73.2", {"start": v(57.54, -12.74) * mm, "end": v(59.49, -13.32) * mm});
            skLineSegment(sketch, "E11.73.3", {"start": v(57.85, -11.25) * mm, "end": v(57.54, -12.74) * mm});
            skLineSegment(sketch, "E11.74.0", {"start": v(60.47, -7.7) * mm, "end": v(58.44, -7.6) * mm});
            skLineSegment(sketch, "E11.74.1", {"start": v(60.47, -7.7) * mm, "end": v(60.2, -9.56) * mm});
            skLineSegment(sketch, "E11.74.2", {"start": v(58.23, -9.1) * mm, "end": v(60.2, -9.56) * mm});
            skLineSegment(sketch, "E11.74.3", {"start": v(58.44, -7.6) * mm, "end": v(58.23, -9.1) * mm});
            skLineSegment(sketch, "E11.75.0", {"start": v(60.84, -3.9) * mm, "end": v(58.8, -3.9) * mm});
            skLineSegment(sketch, "E11.75.1", {"start": v(60.84, -3.9) * mm, "end": v(60.69, -5.76) * mm});
            skLineSegment(sketch, "E11.75.2", {"start": v(58.68, -5.43) * mm, "end": v(60.69, -5.76) * mm});
            skLineSegment(sketch, "E11.75.3", {"start": v(58.8, -3.9) * mm, "end": v(58.68, -5.43) * mm});
            skLineSegment(sketch, "E11.76.0", {"start": v(60.96, -0.06) * mm, "end": v(58.93, -0.2) * mm});
            skLineSegment(sketch, "E11.76.1", {"start": v(60.96, -0.06) * mm, "end": v(60.93, -1.94) * mm});
            skLineSegment(sketch, "E11.76.2", {"start": v(58.9, -1.73) * mm, "end": v(60.93, -1.94) * mm});
            skLineSegment(sketch, "E11.76.3", {"start": v(58.93, -0.2) * mm, "end": v(58.9, -1.73) * mm});
            skLineSegment(sketch, "E11.77.0", {"start": v(60.84, 3.76) * mm, "end": v(58.83, 3.5) * mm});
            skLineSegment(sketch, "E11.77.1", {"start": v(60.84, 3.76) * mm, "end": v(60.93, 1.89) * mm});
            skLineSegment(sketch, "E11.77.2", {"start": v(58.9, 1.97) * mm, "end": v(60.93, 1.89) * mm});
            skLineSegment(sketch, "E11.77.3", {"start": v(58.83, 3.5) * mm, "end": v(58.9, 1.97) * mm});
            skLineSegment(sketch, "E11.78.0", {"start": v(60.49, 7.58) * mm, "end": v(58.5, 7.18) * mm});
            skLineSegment(sketch, "E11.78.1", {"start": v(60.49, 7.58) * mm, "end": v(60.7, 5.71) * mm});
            skLineSegment(sketch, "E11.78.2", {"start": v(58.66, 5.67) * mm, "end": v(60.7, 5.71) * mm});
            skLineSegment(sketch, "E11.78.3", {"start": v(58.5, 7.18) * mm, "end": v(58.66, 5.67) * mm});
            skLineSegment(sketch, "E11.79.0", {"start": v(59.9, 11.36) * mm, "end": v(57.93, 10.84) * mm});
            skLineSegment(sketch, "E11.79.1", {"start": v(59.9, 11.36) * mm, "end": v(60.21, 9.51) * mm});
            skLineSegment(sketch, "E11.79.2", {"start": v(58.19, 9.34) * mm, "end": v(60.21, 9.51) * mm});
            skLineSegment(sketch, "E11.79.3", {"start": v(57.93, 10.84) * mm, "end": v(58.19, 9.34) * mm});
            skPoint(sketch, "E11.center", {"position": v(0, 0) * mm});
            skLineSegment(sketch, "E12.2.80.0", {"start": v(59.06, 15.1) * mm, "end": v(57.13, 14.46) * mm});
            skLineSegment(sketch, "E12.3.80.0", {"start": v(59.06, 15.1) * mm, "end": v(59.5, 13.27) * mm});
            skLineSegment(sketch, "E12.6.80.0", {"start": v(57.49, 12.97) * mm, "end": v(59.5, 13.27) * mm});
            skLineSegment(sketch, "E12.9.80.0", {"start": v(57.13, 14.46) * mm, "end": v(57.49, 12.97) * mm});
            skLineSegment(sketch, "E12.2.81.0", {"start": v(58, 18.78) * mm, "end": v(56.11, 18.01) * mm});
            skLineSegment(sketch, "E12.3.81.0", {"start": v(58, 18.78) * mm, "end": v(58.55, 16.98) * mm});
            skLineSegment(sketch, "E12.6.81.0", {"start": v(56.56, 16.56) * mm, "end": v(58.55, 16.98) * mm});
            skLineSegment(sketch, "E12.9.81.0", {"start": v(56.11, 18.01) * mm, "end": v(56.56, 16.56) * mm});
            skLineSegment(sketch, "E12.2.82.0", {"start": v(56.7, 22.38) * mm, "end": v(54.87, 21.5) * mm});
            skLineSegment(sketch, "E12.3.82.0", {"start": v(56.7, 22.38) * mm, "end": v(57.37, 20.62) * mm});
            skLineSegment(sketch, "E12.6.82.0", {"start": v(55.4, 20.08) * mm, "end": v(57.37, 20.62) * mm});
            skLineSegment(sketch, "E12.9.82.0", {"start": v(54.87, 21.5) * mm, "end": v(55.4, 20.08) * mm});
            skLineSegment(sketch, "E12.2.83.0", {"start": v(55.19, 25.9) * mm, "end": v(53.41, 24.9) * mm});
            skLineSegment(sketch, "E12.3.83.0", {"start": v(55.19, 25.9) * mm, "end": v(55.96, 24.19) * mm});
            skLineSegment(sketch, "E12.6.83.0", {"start": v(54.04, 23.52) * mm, "end": v(55.96, 24.19) * mm});
            skLineSegment(sketch, "E12.9.83.0", {"start": v(53.41, 24.9) * mm, "end": v(54.04, 23.52) * mm});
            skLineSegment(sketch, "E12.2.84.0", {"start": v(53.45, 29.31) * mm, "end": v(51.74, 28.2) * mm});
            skLineSegment(sketch, "E12.3.84.0", {"start": v(53.45, 29.31) * mm, "end": v(54.33, 27.65) * mm});
            skLineSegment(sketch, "E12.6.84.0", {"start": v(52.46, 26.86) * mm, "end": v(54.33, 27.65) * mm});
            skLineSegment(sketch, "E12.9.84.0", {"start": v(51.74, 28.2) * mm, "end": v(52.46, 26.86) * mm});
            skLineSegment(sketch, "E12.2.85.0", {"start": v(51.5, 32.61) * mm, "end": v(49.87, 31.4) * mm});
            skLineSegment(sketch, "E12.3.85.0", {"start": v(51.5, 32.61) * mm, "end": v(52.48, 31) * mm});
            skLineSegment(sketch, "E12.6.85.0", {"start": v(50.67, 30.1) * mm, "end": v(52.48, 31) * mm});
            skLineSegment(sketch, "E12.9.85.0", {"start": v(49.87, 31.4) * mm, "end": v(50.67, 30.1) * mm});
            skLineSegment(sketch, "E12.2.86.0", {"start": v(49.35, 35.78) * mm, "end": v(47.8, 34.47) * mm});
            skLineSegment(sketch, "E12.3.86.0", {"start": v(49.35, 35.78) * mm, "end": v(50.43, 34.24) * mm});
            skLineSegment(sketch, "E12.6.86.0", {"start": v(48.67, 33.23) * mm, "end": v(50.43, 34.24) * mm});
            skLineSegment(sketch, "E12.9.86.0", {"start": v(47.8, 34.47) * mm, "end": v(48.67, 33.23) * mm});
            skLineSegment(sketch, "E12.2.87.0", {"start": v(47.01, 38.8) * mm, "end": v(45.54, 37.4) * mm});
            skLineSegment(sketch, "E12.3.87.0", {"start": v(47.01, 38.8) * mm, "end": v(48.18, 37.34) * mm});
            skLineSegment(sketch, "E12.6.87.0", {"start": v(46.5, 36.22) * mm, "end": v(48.18, 37.34) * mm});
            skLineSegment(sketch, "E12.9.87.0", {"start": v(45.54, 37.4) * mm, "end": v(46.5, 36.22) * mm});
            skLineSegment(sketch, "E12.2.88.0", {"start": v(44.48, 41.68) * mm, "end": v(43.1, 40.2) * mm});
            skLineSegment(sketch, "E12.3.88.0", {"start": v(44.48, 41.68) * mm, "end": v(45.74, 40.3) * mm});
            skLineSegment(sketch, "E12.6.88.0", {"start": v(44.13, 39.06) * mm, "end": v(45.74, 40.3) * mm});
            skLineSegment(sketch, "E12.9.88.0", {"start": v(43.1, 40.2) * mm, "end": v(44.13, 39.06) * mm});
            skLineSegment(sketch, "E12.2.89.0", {"start": v(41.78, 44.4) * mm, "end": v(40.5, 42.82) * mm});
            skLineSegment(sketch, "E12.3.89.0", {"start": v(41.78, 44.4) * mm, "end": v(43.12, 43.09) * mm});
            skLineSegment(sketch, "E12.6.89.0", {"start": v(41.59, 41.76) * mm, "end": v(43.12, 43.09) * mm});
            skLineSegment(sketch, "E12.9.89.0", {"start": v(40.5, 42.82) * mm, "end": v(41.59, 41.76) * mm});
            skLineSegment(sketch, "E12.2.90.0", {"start": v(38.9, 46.93) * mm, "end": v(37.72, 45.28) * mm});
            skLineSegment(sketch, "E12.3.90.0", {"start": v(38.9, 46.93) * mm, "end": v(40.33, 45.7) * mm});
            skLineSegment(sketch, "E12.6.90.0", {"start": v(38.88, 44.29) * mm, "end": v(40.33, 45.7) * mm});
            skLineSegment(sketch, "E12.9.90.0", {"start": v(37.72, 45.28) * mm, "end": v(38.88, 44.29) * mm});
            skLineSegment(sketch, "E12.2.91.0", {"start": v(35.88, 49.28) * mm, "end": v(34.8, 47.56) * mm});
            skLineSegment(sketch, "E12.3.91.0", {"start": v(35.88, 49.28) * mm, "end": v(37.38, 48.15) * mm});
            skLineSegment(sketch, "E12.6.91.0", {"start": v(36.03, 46.64) * mm, "end": v(37.38, 48.15) * mm});
            skLineSegment(sketch, "E12.9.91.0", {"start": v(34.8, 47.56) * mm, "end": v(36.03, 46.64) * mm});
            skLineSegment(sketch, "E12.2.92.0", {"start": v(32.72, 51.44) * mm, "end": v(31.75, 49.65) * mm});
            skLineSegment(sketch, "E12.3.92.0", {"start": v(32.72, 51.44) * mm, "end": v(34.29, 50.4) * mm});
            skLineSegment(sketch, "E12.6.92.0", {"start": v(33.03, 48.81) * mm, "end": v(34.29, 50.4) * mm});
            skLineSegment(sketch, "E12.9.92.0", {"start": v(31.75, 49.65) * mm, "end": v(33.03, 48.81) * mm});
            skLineSegment(sketch, "E12.2.93.0", {"start": v(29.42, 53.39) * mm, "end": v(28.57, 51.54) * mm});
            skLineSegment(sketch, "E12.3.93.0", {"start": v(29.42, 53.39) * mm, "end": v(31.05, 52.46) * mm});
            skLineSegment(sketch, "E12.6.93.0", {"start": v(29.9, 50.79) * mm, "end": v(31.05, 52.46) * mm});
            skLineSegment(sketch, "E12.9.93.0", {"start": v(28.57, 51.54) * mm, "end": v(29.9, 50.79) * mm});
            skLineSegment(sketch, "E12.2.94.0", {"start": v(26.01, 55.13) * mm, "end": v(25.28, 53.24) * mm});
            skLineSegment(sketch, "E12.3.94.0", {"start": v(26.01, 55.13) * mm, "end": v(27.7, 54.3) * mm});
            skLineSegment(sketch, "E12.6.94.0", {"start": v(26.65, 52.56) * mm, "end": v(27.7, 54.3) * mm});
            skLineSegment(sketch, "E12.9.94.0", {"start": v(25.28, 53.24) * mm, "end": v(26.65, 52.56) * mm});
            skLineSegment(sketch, "E12.2.95.0", {"start": v(22.5, 56.66) * mm, "end": v(21.89, 54.72) * mm});
            skLineSegment(sketch, "E12.3.95.0", {"start": v(22.5, 56.66) * mm, "end": v(24.23, 55.94) * mm});
            skLineSegment(sketch, "E12.6.95.0", {"start": v(23.3, 54.13) * mm, "end": v(24.23, 55.94) * mm});
            skLineSegment(sketch, "E12.9.95.0", {"start": v(21.89, 54.72) * mm, "end": v(23.3, 54.13) * mm});
            skLineSegment(sketch, "E12.2.96.0", {"start": v(18.9, 57.96) * mm, "end": v(18.4, 55.98) * mm});
            skLineSegment(sketch, "E12.3.96.0", {"start": v(18.9, 57.96) * mm, "end": v(20.67, 57.35) * mm});
            skLineSegment(sketch, "E12.6.96.0", {"start": v(19.85, 55.5) * mm, "end": v(20.67, 57.35) * mm});
            skLineSegment(sketch, "E12.9.96.0", {"start": v(18.4, 55.98) * mm, "end": v(19.85, 55.5) * mm});
            skLineSegment(sketch, "E12.2.97.0", {"start": v(15.22, 59.03) * mm, "end": v(14.86, 57.03) * mm});
            skLineSegment(sketch, "E12.3.97.0", {"start": v(15.22, 59.03) * mm, "end": v(17.03, 58.53) * mm});
            skLineSegment(sketch, "E12.6.97.0", {"start": v(16.33, 56.63) * mm, "end": v(17.03, 58.53) * mm});
            skLineSegment(sketch, "E12.9.97.0", {"start": v(14.86, 57.03) * mm, "end": v(16.33, 56.63) * mm});
            skLineSegment(sketch, "E12.2.98.0", {"start": v(11.48, 59.87) * mm, "end": v(11.25, 57.85) * mm});
            skLineSegment(sketch, "E12.3.98.0", {"start": v(11.48, 59.87) * mm, "end": v(13.32, 59.49) * mm});
            skLineSegment(sketch, "E12.6.98.0", {"start": v(12.74, 57.54) * mm, "end": v(13.32, 59.49) * mm});
            skLineSegment(sketch, "E12.9.98.0", {"start": v(11.25, 57.85) * mm, "end": v(12.74, 57.54) * mm});
            skLineSegment(sketch, "E12.2.99.0", {"start": v(7.7, 60.47) * mm, "end": v(7.6, 58.44) * mm});
            skLineSegment(sketch, "E12.3.99.0", {"start": v(7.7, 60.47) * mm, "end": v(9.56, 60.2) * mm});
            skLineSegment(sketch, "E12.6.99.0", {"start": v(9.1, 58.23) * mm, "end": v(9.56, 60.2) * mm});
            skLineSegment(sketch, "E12.9.99.0", {"start": v(7.6, 58.44) * mm, "end": v(9.1, 58.23) * mm});
            skSolve(sketch);
        }
        {
            var Q0;
            Q0 = qSketchRegion(id + "F6", true);
            extrude(context, id + "F7", {"entities" : qUnion([Q0]), "oppositeDirection" : true, "depth" : 10.16 * mm});
        }
        {
            var Q0;
            {var subQ0=sQuery(id+"F0.wireOp",EDGE,"E0");Q0=makeQuery(id+"F5.boolean.opBoolean","SPLIT",FACE,{"disambiguationData":[TD([makeQuery(id+"F2.opFillet","BLEND_FACE",FACE,{"disambiguationData":[OSD([subQ0])]})])],"derivedFrom":makeQuery(id+"F1.opExtrude","CAP_FACE",FACE,{"disambiguationData":[OSD([subQ0,sQuery(id+"F0.wireOp",EDGE,"E1")])],"isStart":false})});}
            var sketch = newSketch(context, id + "F8", { "sketchPlane" : qUnion([Q0])});
            skLineSegment(sketch, "E13", {"start": v(0, 71.12) * mm, "end": v(0, 74.23) * mm, "construction": true});
            skLineSegment(sketch, "E14", {"start": v(0, 74.23) * mm, "end": v(5.1, 76.22) * mm});
            skLineSegment(sketch, "E15", {"start": v(5.1, 76.22) * mm, "end": v(0.63, 76.66) * mm});
            skLineSegment(sketch, "E16", {"start": v(0.63, 76.66) * mm, "end": v(9.07, 76.72) * mm});
            skLineSegment(sketch, "E17", {"start": v(9.07, 76.72) * mm, "end": v(0, 73.9) * mm});
            skLineSegment(sketch, "E18", {"start": v(0, 73.9) * mm, "end": v(0, 74.23) * mm});
            skLineSegment(sketch, "E19.1.0", {"start": v(-4.38, 76.53) * mm, "end": v(4.04, 77.15) * mm});
            skLineSegment(sketch, "E19.1.1", {"start": v(0.1, 76.39) * mm, "end": v(-4.38, 76.53) * mm});
            skLineSegment(sketch, "E19.1.2", {"start": v(4.04, 77.15) * mm, "end": v(-4.83, 73.74) * mm});
            skLineSegment(sketch, "E19.1.3", {"start": v(-4.85, 74.07) * mm, "end": v(0.1, 76.39) * mm});
            skLineSegment(sketch, "E19.1.4", {"start": v(-4.83, 73.74) * mm, "end": v(-4.85, 74.07) * mm});
            skPoint(sketch, "E19.center", {"position": v(0, 0) * mm});
            skLineSegment(sketch, "E20.1.2.0", {"start": v(-9.38, 76.08) * mm, "end": v(-1.02, 77.24) * mm});
            skLineSegment(sketch, "E20.3.2.0", {"start": v(-4.89, 76.23) * mm, "end": v(-9.38, 76.08) * mm});
            skLineSegment(sketch, "E20.6.2.0", {"start": v(-1.02, 77.24) * mm, "end": v(-9.65, 73.27) * mm});
            skLineSegment(sketch, "E20.9.2.0", {"start": v(-9.69, 73.6) * mm, "end": v(-4.89, 76.23) * mm});
            skLineSegment(sketch, "E20.12.2.0", {"start": v(-9.65, 73.27) * mm, "end": v(-9.69, 73.6) * mm});
            skLineSegment(sketch, "E20.1.3.0", {"start": v(-14.33, 75.3) * mm, "end": v(-6.07, 77.01) * mm});
            skLineSegment(sketch, "E20.3.3.0", {"start": v(-9.86, 75.75) * mm, "end": v(-14.33, 75.3) * mm});
            skLineSegment(sketch, "E20.6.3.0", {"start": v(-6.07, 77.01) * mm, "end": v(-14.42, 72.48) * mm});
            skLineSegment(sketch, "E20.9.3.0", {"start": v(-14.48, 72.8) * mm, "end": v(-9.86, 75.75) * mm});
            skLineSegment(sketch, "E20.12.3.0", {"start": v(-14.42, 72.48) * mm, "end": v(-14.48, 72.8) * mm});
            skLineSegment(sketch, "E20.1.4.0", {"start": v(-19.23, 74.2) * mm, "end": v(-11.1, 76.45) * mm});
            skLineSegment(sketch, "E20.3.4.0", {"start": v(-14.8, 74.94) * mm, "end": v(-19.23, 74.2) * mm});
            skLineSegment(sketch, "E20.6.4.0", {"start": v(-11.1, 76.45) * mm, "end": v(-19.13, 71.38) * mm});
            skLineSegment(sketch, "E20.9.4.0", {"start": v(-19.21, 71.7) * mm, "end": v(-14.8, 74.94) * mm});
            skLineSegment(sketch, "E20.12.4.0", {"start": v(-19.13, 71.38) * mm, "end": v(-19.21, 71.7) * mm});
            skLineSegment(sketch, "E20.1.5.0", {"start": v(-24.04, 72.8) * mm, "end": v(-16.07, 75.56) * mm});
            skLineSegment(sketch, "E20.3.5.0", {"start": v(-19.67, 73.81) * mm, "end": v(-24.04, 72.8) * mm});
            skLineSegment(sketch, "E20.6.5.0", {"start": v(-16.07, 75.56) * mm, "end": v(-23.75, 69.98) * mm});
            skLineSegment(sketch, "E20.9.5.0", {"start": v(-23.86, 70.3) * mm, "end": v(-19.67, 73.81) * mm});
            skLineSegment(sketch, "E20.12.5.0", {"start": v(-23.75, 69.98) * mm, "end": v(-23.86, 70.3) * mm});
            skLineSegment(sketch, "E20.1.6.0", {"start": v(-28.75, 71.06) * mm, "end": v(-20.97, 74.35) * mm});
            skLineSegment(sketch, "E20.3.6.0", {"start": v(-24.45, 72.37) * mm, "end": v(-28.75, 71.06) * mm});
            skLineSegment(sketch, "E20.6.6.0", {"start": v(-20.97, 74.35) * mm, "end": v(-28.28, 68.28) * mm});
            skLineSegment(sketch, "E20.9.6.0", {"start": v(-28.4, 68.58) * mm, "end": v(-24.45, 72.37) * mm});
            skLineSegment(sketch, "E20.12.6.0", {"start": v(-28.28, 68.28) * mm, "end": v(-28.4, 68.58) * mm});
            skLineSegment(sketch, "E20.1.7.0", {"start": v(-33.34, 69.03) * mm, "end": v(-25.8, 72.82) * mm});
            skLineSegment(sketch, "E20.3.7.0", {"start": v(-29.13, 70.61) * mm, "end": v(-33.34, 69.03) * mm});
            skLineSegment(sketch, "E20.6.7.0", {"start": v(-25.8, 72.82) * mm, "end": v(-32.69, 66.28) * mm});
            skLineSegment(sketch, "E20.9.7.0", {"start": v(-32.83, 66.58) * mm, "end": v(-29.13, 70.61) * mm});
            skLineSegment(sketch, "E20.12.7.0", {"start": v(-32.69, 66.28) * mm, "end": v(-32.83, 66.58) * mm});
            skLineSegment(sketch, "E20.1.8.0", {"start": v(-37.78, 66.7) * mm, "end": v(-30.5, 70.97) * mm});
            skLineSegment(sketch, "E20.3.8.0", {"start": v(-33.69, 68.56) * mm, "end": v(-37.78, 66.7) * mm});
            skLineSegment(sketch, "E20.6.8.0", {"start": v(-30.5, 70.97) * mm, "end": v(-36.95, 64) * mm});
            skLineSegment(sketch, "E20.9.8.0", {"start": v(-37.12, 64.29) * mm, "end": v(-33.69, 68.56) * mm});
            skLineSegment(sketch, "E20.12.8.0", {"start": v(-36.95, 64) * mm, "end": v(-37.12, 64.29) * mm});
            skLineSegment(sketch, "E20.1.9.0", {"start": v(-42.06, 64.09) * mm, "end": v(-35.08, 68.83) * mm});
            skLineSegment(sketch, "E20.3.9.0", {"start": v(-38.1, 66.2) * mm, "end": v(-42.06, 64.09) * mm});
            skLineSegment(sketch, "E20.6.9.0", {"start": v(-35.08, 68.83) * mm, "end": v(-41.06, 61.45) * mm});
            skLineSegment(sketch, "E20.9.9.0", {"start": v(-41.24, 61.72) * mm, "end": v(-38.1, 66.2) * mm});
            skLineSegment(sketch, "E20.12.9.0", {"start": v(-41.06, 61.45) * mm, "end": v(-41.24, 61.72) * mm});
            skLineSegment(sketch, "E20.1.10.0", {"start": v(-46.16, 61.2) * mm, "end": v(-39.5, 66.39) * mm});
            skLineSegment(sketch, "E20.3.10.0", {"start": v(-42.35, 63.57) * mm, "end": v(-46.16, 61.2) * mm});
            skLineSegment(sketch, "E20.6.10.0", {"start": v(-39.5, 66.39) * mm, "end": v(-44.99, 58.63) * mm});
            skLineSegment(sketch, "E20.9.10.0", {"start": v(-45.19, 58.9) * mm, "end": v(-42.35, 63.57) * mm});
            skLineSegment(sketch, "E20.12.10.0", {"start": v(-44.99, 58.63) * mm, "end": v(-45.19, 58.9) * mm});
            skLineSegment(sketch, "E20.1.11.0", {"start": v(-50.07, 58.05) * mm, "end": v(-43.76, 63.66) * mm});
            skLineSegment(sketch, "E20.3.11.0", {"start": v(-46.42, 60.67) * mm, "end": v(-50.07, 58.05) * mm});
            skLineSegment(sketch, "E20.6.11.0", {"start": v(-43.76, 63.66) * mm, "end": v(-48.73, 55.56) * mm});
            skLineSegment(sketch, "E20.9.11.0", {"start": v(-48.94, 55.81) * mm, "end": v(-46.42, 60.67) * mm});
            skLineSegment(sketch, "E20.12.11.0", {"start": v(-48.73, 55.56) * mm, "end": v(-48.94, 55.81) * mm});
            skLineSegment(sketch, "E20.1.12.0", {"start": v(-53.76, 54.65) * mm, "end": v(-47.83, 60.66) * mm});
            skLineSegment(sketch, "E20.3.12.0", {"start": v(-50.28, 57.5) * mm, "end": v(-53.76, 54.65) * mm});
            skLineSegment(sketch, "E20.6.12.0", {"start": v(-47.83, 60.66) * mm, "end": v(-52.26, 52.26) * mm});
            skLineSegment(sketch, "E20.9.12.0", {"start": v(-52.49, 52.49) * mm, "end": v(-50.28, 57.5) * mm});
            skLineSegment(sketch, "E20.12.12.0", {"start": v(-52.26, 52.26) * mm, "end": v(-52.49, 52.49) * mm});
            skLineSegment(sketch, "E20.1.13.0", {"start": v(-57.22, 51.02) * mm, "end": v(-51.7, 57.4) * mm});
            skLineSegment(sketch, "E20.3.13.0", {"start": v(-53.94, 54.1) * mm, "end": v(-57.22, 51.02) * mm});
            skLineSegment(sketch, "E20.6.13.0", {"start": v(-51.7, 57.4) * mm, "end": v(-55.56, 48.73) * mm});
            skLineSegment(sketch, "E20.9.13.0", {"start": v(-55.81, 48.94) * mm, "end": v(-53.94, 54.1) * mm});
            skLineSegment(sketch, "E20.12.13.0", {"start": v(-55.56, 48.73) * mm, "end": v(-55.81, 48.94) * mm});
            skLineSegment(sketch, "E20.1.14.0", {"start": v(-60.43, 47.17) * mm, "end": v(-55.34, 53.9) * mm});
            skLineSegment(sketch, "E20.3.14.0", {"start": v(-57.36, 50.45) * mm, "end": v(-60.43, 47.17) * mm});
            skLineSegment(sketch, "E20.6.14.0", {"start": v(-55.34, 53.9) * mm, "end": v(-58.63, 44.99) * mm});
            skLineSegment(sketch, "E20.9.14.0", {"start": v(-58.9, 45.19) * mm, "end": v(-57.36, 50.45) * mm});
            skLineSegment(sketch, "E20.12.14.0", {"start": v(-58.63, 44.99) * mm, "end": v(-58.9, 45.19) * mm});
            skLineSegment(sketch, "E20.1.15.0", {"start": v(-63.39, 43.11) * mm, "end": v(-58.75, 50.17) * mm});
            skLineSegment(sketch, "E20.3.15.0", {"start": v(-60.54, 46.59) * mm, "end": v(-63.39, 43.11) * mm});
            skLineSegment(sketch, "E20.6.15.0", {"start": v(-58.75, 50.17) * mm, "end": v(-61.45, 41.06) * mm});
            skLineSegment(sketch, "E20.9.15.0", {"start": v(-61.72, 41.24) * mm, "end": v(-60.54, 46.59) * mm});
            skLineSegment(sketch, "E20.12.15.0", {"start": v(-61.45, 41.06) * mm, "end": v(-61.72, 41.24) * mm});
            skLineSegment(sketch, "E20.1.16.0", {"start": v(-66.07, 38.88) * mm, "end": v(-61.9, 46.22) * mm});
            skLineSegment(sketch, "E20.3.16.0", {"start": v(-63.45, 42.53) * mm, "end": v(-66.07, 38.88) * mm});
            skLineSegment(sketch, "E20.6.16.0", {"start": v(-61.9, 46.22) * mm, "end": v(-64, 36.95) * mm});
            skLineSegment(sketch, "E20.9.16.0", {"start": v(-64.29, 37.12) * mm, "end": v(-63.45, 42.53) * mm});
            skLineSegment(sketch, "E20.12.16.0", {"start": v(-64, 36.95) * mm, "end": v(-64.29, 37.12) * mm});
            skLineSegment(sketch, "E20.1.17.0", {"start": v(-68.47, 34.47) * mm, "end": v(-64.8, 42.07) * mm});
            skLineSegment(sketch, "E20.3.17.0", {"start": v(-66.1, 38.29) * mm, "end": v(-68.47, 34.47) * mm});
            skLineSegment(sketch, "E20.6.17.0", {"start": v(-64.8, 42.07) * mm, "end": v(-66.28, 32.69) * mm});
            skLineSegment(sketch, "E20.9.17.0", {"start": v(-66.58, 32.83) * mm, "end": v(-66.1, 38.29) * mm});
            skLineSegment(sketch, "E20.12.17.0", {"start": v(-66.28, 32.69) * mm, "end": v(-66.58, 32.83) * mm});
            skLineSegment(sketch, "E20.1.18.0", {"start": v(-70.58, 29.92) * mm, "end": v(-67.4, 37.74) * mm});
            skLineSegment(sketch, "E20.3.18.0", {"start": v(-68.46, 33.88) * mm, "end": v(-70.58, 29.92) * mm});
            skLineSegment(sketch, "E20.6.18.0", {"start": v(-67.4, 37.74) * mm, "end": v(-68.28, 28.28) * mm});
            skLineSegment(sketch, "E20.9.18.0", {"start": v(-68.58, 28.4) * mm, "end": v(-68.46, 33.88) * mm});
            skLineSegment(sketch, "E20.12.18.0", {"start": v(-68.28, 28.28) * mm, "end": v(-68.58, 28.4) * mm});
            skLineSegment(sketch, "E20.1.19.0", {"start": v(-72.38, 25.24) * mm, "end": v(-69.73, 33.25) * mm});
            skLineSegment(sketch, "E20.3.19.0", {"start": v(-70.53, 29.33) * mm, "end": v(-72.38, 25.24) * mm});
            skLineSegment(sketch, "E20.6.19.0", {"start": v(-69.73, 33.25) * mm, "end": v(-69.98, 23.75) * mm});
            skLineSegment(sketch, "E20.9.19.0", {"start": v(-70.3, 23.86) * mm, "end": v(-70.53, 29.33) * mm});
            skLineSegment(sketch, "E20.12.19.0", {"start": v(-69.98, 23.75) * mm, "end": v(-70.3, 23.86) * mm});
            skLineSegment(sketch, "E20.1.20.0", {"start": v(-73.88, 20.45) * mm, "end": v(-71.75, 28.62) * mm});
            skLineSegment(sketch, "E20.3.20.0", {"start": v(-72.3, 24.66) * mm, "end": v(-73.88, 20.45) * mm});
            skLineSegment(sketch, "E20.6.20.0", {"start": v(-71.75, 28.62) * mm, "end": v(-71.38, 19.13) * mm});
            skLineSegment(sketch, "E20.9.20.0", {"start": v(-71.7, 19.21) * mm, "end": v(-72.3, 24.66) * mm});
            skLineSegment(sketch, "E20.12.20.0", {"start": v(-71.38, 19.13) * mm, "end": v(-71.7, 19.21) * mm});
            skLineSegment(sketch, "E20.1.21.0", {"start": v(-75.06, 15.58) * mm, "end": v(-73.47, 23.87) * mm});
            skLineSegment(sketch, "E20.3.21.0", {"start": v(-73.76, 19.88) * mm, "end": v(-75.06, 15.58) * mm});
            skLineSegment(sketch, "E20.6.21.0", {"start": v(-73.47, 23.87) * mm, "end": v(-72.48, 14.42) * mm});
            skLineSegment(sketch, "E20.9.21.0", {"start": v(-72.8, 14.48) * mm, "end": v(-73.76, 19.88) * mm});
            skLineSegment(sketch, "E20.12.21.0", {"start": v(-72.48, 14.42) * mm, "end": v(-72.8, 14.48) * mm});
            skLineSegment(sketch, "E20.1.22.0", {"start": v(-75.92, 10.63) * mm, "end": v(-74.88, 19) * mm});
            skLineSegment(sketch, "E20.3.22.0", {"start": v(-74.9, 15) * mm, "end": v(-75.92, 10.63) * mm});
            skLineSegment(sketch, "E20.6.22.0", {"start": v(-74.88, 19) * mm, "end": v(-73.27, 9.65) * mm});
            skLineSegment(sketch, "E20.9.22.0", {"start": v(-73.6, 9.69) * mm, "end": v(-74.9, 15) * mm});
            skLineSegment(sketch, "E20.12.22.0", {"start": v(-73.27, 9.65) * mm, "end": v(-73.6, 9.69) * mm});
            skLineSegment(sketch, "E20.1.23.0", {"start": v(-76.45, 5.64) * mm, "end": v(-75.96, 14.07) * mm});
            skLineSegment(sketch, "E20.3.23.0", {"start": v(-75.72, 10.08) * mm, "end": v(-76.45, 5.64) * mm});
            skLineSegment(sketch, "E20.6.23.0", {"start": v(-75.96, 14.07) * mm, "end": v(-73.74, 4.83) * mm});
            skLineSegment(sketch, "E20.9.23.0", {"start": v(-74.07, 4.85) * mm, "end": v(-75.72, 10.08) * mm});
            skLineSegment(sketch, "E20.12.23.0", {"start": v(-73.74, 4.83) * mm, "end": v(-74.07, 4.85) * mm});
            skLineSegment(sketch, "E20.1.24.0", {"start": v(-76.66, 0.63) * mm, "end": v(-76.72, 9.07) * mm});
            skLineSegment(sketch, "E20.3.24.0", {"start": v(-76.22, 5.1) * mm, "end": v(-76.66, 0.63) * mm});
            skLineSegment(sketch, "E20.6.24.0", {"start": v(-76.72, 9.07) * mm, "end": v(-73.9, 0) * mm});
            skLineSegment(sketch, "E20.9.24.0", {"start": v(-74.23, 0) * mm, "end": v(-76.22, 5.1) * mm});
            skLineSegment(sketch, "E20.12.24.0", {"start": v(-73.9, 0) * mm, "end": v(-74.23, 0) * mm});
            skLineSegment(sketch, "E20.1.25.0", {"start": v(-76.53, -4.38) * mm, "end": v(-77.15, 4.04) * mm});
            skLineSegment(sketch, "E20.3.25.0", {"start": v(-76.39, 0.1) * mm, "end": v(-76.53, -4.38) * mm});
            skLineSegment(sketch, "E20.6.25.0", {"start": v(-77.15, 4.04) * mm, "end": v(-73.74, -4.83) * mm});
            skLineSegment(sketch, "E20.9.25.0", {"start": v(-74.07, -4.85) * mm, "end": v(-76.39, 0.1) * mm});
            skLineSegment(sketch, "E20.12.25.0", {"start": v(-73.74, -4.83) * mm, "end": v(-74.07, -4.85) * mm});
            skLineSegment(sketch, "E20.1.26.0", {"start": v(-76.08, -9.38) * mm, "end": v(-77.24, -1.02) * mm});
            skLineSegment(sketch, "E20.3.26.0", {"start": v(-76.23, -4.89) * mm, "end": v(-76.08, -9.38) * mm});
            skLineSegment(sketch, "E20.6.26.0", {"start": v(-77.24, -1.02) * mm, "end": v(-73.27, -9.65) * mm});
            skLineSegment(sketch, "E20.9.26.0", {"start": v(-73.6, -9.69) * mm, "end": v(-76.23, -4.89) * mm});
            skLineSegment(sketch, "E20.12.26.0", {"start": v(-73.27, -9.65) * mm, "end": v(-73.6, -9.69) * mm});
            skLineSegment(sketch, "E20.1.27.0", {"start": v(-75.3, -14.33) * mm, "end": v(-77.01, -6.07) * mm});
            skLineSegment(sketch, "E20.3.27.0", {"start": v(-75.75, -9.86) * mm, "end": v(-75.3, -14.33) * mm});
            skLineSegment(sketch, "E20.6.27.0", {"start": v(-77.01, -6.07) * mm, "end": v(-72.48, -14.42) * mm});
            skLineSegment(sketch, "E20.9.27.0", {"start": v(-72.8, -14.48) * mm, "end": v(-75.75, -9.86) * mm});
            skLineSegment(sketch, "E20.12.27.0", {"start": v(-72.48, -14.42) * mm, "end": v(-72.8, -14.48) * mm});
            skLineSegment(sketch, "E20.1.28.0", {"start": v(-74.2, -19.23) * mm, "end": v(-76.45, -11.1) * mm});
            skLineSegment(sketch, "E20.3.28.0", {"start": v(-74.94, -14.8) * mm, "end": v(-74.2, -19.23) * mm});
            skLineSegment(sketch, "E20.6.28.0", {"start": v(-76.45, -11.1) * mm, "end": v(-71.38, -19.13) * mm});
            skLineSegment(sketch, "E20.9.28.0", {"start": v(-71.7, -19.21) * mm, "end": v(-74.94, -14.8) * mm});
            skLineSegment(sketch, "E20.12.28.0", {"start": v(-71.38, -19.13) * mm, "end": v(-71.7, -19.21) * mm});
            skLineSegment(sketch, "E20.1.29.0", {"start": v(-72.8, -24.04) * mm, "end": v(-75.56, -16.07) * mm});
            skLineSegment(sketch, "E20.3.29.0", {"start": v(-73.81, -19.67) * mm, "end": v(-72.8, -24.04) * mm});
            skLineSegment(sketch, "E20.6.29.0", {"start": v(-75.56, -16.07) * mm, "end": v(-69.98, -23.75) * mm});
            skLineSegment(sketch, "E20.9.29.0", {"start": v(-70.3, -23.86) * mm, "end": v(-73.81, -19.67) * mm});
            skLineSegment(sketch, "E20.12.29.0", {"start": v(-69.98, -23.75) * mm, "end": v(-70.3, -23.86) * mm});
            skLineSegment(sketch, "E20.1.30.0", {"start": v(-71.06, -28.75) * mm, "end": v(-74.35, -20.97) * mm});
            skLineSegment(sketch, "E20.3.30.0", {"start": v(-72.37, -24.45) * mm, "end": v(-71.06, -28.75) * mm});
            skLineSegment(sketch, "E20.6.30.0", {"start": v(-74.35, -20.97) * mm, "end": v(-68.28, -28.28) * mm});
            skLineSegment(sketch, "E20.9.30.0", {"start": v(-68.58, -28.4) * mm, "end": v(-72.37, -24.45) * mm});
            skLineSegment(sketch, "E20.12.30.0", {"start": v(-68.28, -28.28) * mm, "end": v(-68.58, -28.4) * mm});
            skLineSegment(sketch, "E20.1.31.0", {"start": v(-69.03, -33.34) * mm, "end": v(-72.82, -25.8) * mm});
            skLineSegment(sketch, "E20.3.31.0", {"start": v(-70.61, -29.13) * mm, "end": v(-69.03, -33.34) * mm});
            skLineSegment(sketch, "E20.6.31.0", {"start": v(-72.82, -25.8) * mm, "end": v(-66.28, -32.69) * mm});
            skLineSegment(sketch, "E20.9.31.0", {"start": v(-66.58, -32.83) * mm, "end": v(-70.61, -29.13) * mm});
            skLineSegment(sketch, "E20.12.31.0", {"start": v(-66.28, -32.69) * mm, "end": v(-66.58, -32.83) * mm});
            skLineSegment(sketch, "E20.1.32.0", {"start": v(-66.7, -37.78) * mm, "end": v(-70.97, -30.5) * mm});
            skLineSegment(sketch, "E20.3.32.0", {"start": v(-68.56, -33.69) * mm, "end": v(-66.7, -37.78) * mm});
            skLineSegment(sketch, "E20.6.32.0", {"start": v(-70.97, -30.5) * mm, "end": v(-64, -36.95) * mm});
            skLineSegment(sketch, "E20.9.32.0", {"start": v(-64.29, -37.12) * mm, "end": v(-68.56, -33.69) * mm});
            skLineSegment(sketch, "E20.12.32.0", {"start": v(-64, -36.95) * mm, "end": v(-64.29, -37.12) * mm});
            skLineSegment(sketch, "E20.1.33.0", {"start": v(-64.09, -42.06) * mm, "end": v(-68.83, -35.08) * mm});
            skLineSegment(sketch, "E20.3.33.0", {"start": v(-66.2, -38.1) * mm, "end": v(-64.09, -42.06) * mm});
            skLineSegment(sketch, "E20.6.33.0", {"start": v(-68.83, -35.08) * mm, "end": v(-61.45, -41.06) * mm});
            skLineSegment(sketch, "E20.9.33.0", {"start": v(-61.72, -41.24) * mm, "end": v(-66.2, -38.1) * mm});
            skLineSegment(sketch, "E20.12.33.0", {"start": v(-61.45, -41.06) * mm, "end": v(-61.72, -41.24) * mm});
            skLineSegment(sketch, "E20.1.34.0", {"start": v(-61.2, -46.16) * mm, "end": v(-66.39, -39.5) * mm});
            skLineSegment(sketch, "E20.3.34.0", {"start": v(-63.57, -42.35) * mm, "end": v(-61.2, -46.16) * mm});
            skLineSegment(sketch, "E20.6.34.0", {"start": v(-66.39, -39.5) * mm, "end": v(-58.63, -44.99) * mm});
            skLineSegment(sketch, "E20.9.34.0", {"start": v(-58.9, -45.19) * mm, "end": v(-63.57, -42.35) * mm});
            skLineSegment(sketch, "E20.12.34.0", {"start": v(-58.63, -44.99) * mm, "end": v(-58.9, -45.19) * mm});
            skLineSegment(sketch, "E20.1.35.0", {"start": v(-58.05, -50.07) * mm, "end": v(-63.66, -43.76) * mm});
            skLineSegment(sketch, "E20.3.35.0", {"start": v(-60.67, -46.42) * mm, "end": v(-58.05, -50.07) * mm});
            skLineSegment(sketch, "E20.6.35.0", {"start": v(-63.66, -43.76) * mm, "end": v(-55.56, -48.73) * mm});
            skLineSegment(sketch, "E20.9.35.0", {"start": v(-55.81, -48.94) * mm, "end": v(-60.67, -46.42) * mm});
            skLineSegment(sketch, "E20.12.35.0", {"start": v(-55.56, -48.73) * mm, "end": v(-55.81, -48.94) * mm});
            skLineSegment(sketch, "E20.1.36.0", {"start": v(-54.65, -53.76) * mm, "end": v(-60.66, -47.83) * mm});
            skLineSegment(sketch, "E20.3.36.0", {"start": v(-57.5, -50.28) * mm, "end": v(-54.65, -53.76) * mm});
            skLineSegment(sketch, "E20.6.36.0", {"start": v(-60.66, -47.83) * mm, "end": v(-52.26, -52.26) * mm});
            skLineSegment(sketch, "E20.9.36.0", {"start": v(-52.49, -52.49) * mm, "end": v(-57.5, -50.28) * mm});
            skLineSegment(sketch, "E20.12.36.0", {"start": v(-52.26, -52.26) * mm, "end": v(-52.49, -52.49) * mm});
            skLineSegment(sketch, "E20.1.37.0", {"start": v(-51.02, -57.22) * mm, "end": v(-57.4, -51.7) * mm});
            skLineSegment(sketch, "E20.3.37.0", {"start": v(-54.1, -53.94) * mm, "end": v(-51.02, -57.22) * mm});
            skLineSegment(sketch, "E20.6.37.0", {"start": v(-57.4, -51.7) * mm, "end": v(-48.73, -55.56) * mm});
            skLineSegment(sketch, "E20.9.37.0", {"start": v(-48.94, -55.81) * mm, "end": v(-54.1, -53.94) * mm});
            skLineSegment(sketch, "E20.12.37.0", {"start": v(-48.73, -55.56) * mm, "end": v(-48.94, -55.81) * mm});
            skLineSegment(sketch, "E20.1.38.0", {"start": v(-47.17, -60.43) * mm, "end": v(-53.9, -55.34) * mm});
            skLineSegment(sketch, "E20.3.38.0", {"start": v(-50.45, -57.36) * mm, "end": v(-47.17, -60.43) * mm});
            skLineSegment(sketch, "E20.6.38.0", {"start": v(-53.9, -55.34) * mm, "end": v(-44.99, -58.63) * mm});
            skLineSegment(sketch, "E20.9.38.0", {"start": v(-45.19, -58.9) * mm, "end": v(-50.45, -57.36) * mm});
            skLineSegment(sketch, "E20.12.38.0", {"start": v(-44.99, -58.63) * mm, "end": v(-45.19, -58.9) * mm});
            skLineSegment(sketch, "E20.1.39.0", {"start": v(-43.11, -63.39) * mm, "end": v(-50.17, -58.75) * mm});
            skLineSegment(sketch, "E20.3.39.0", {"start": v(-46.59, -60.54) * mm, "end": v(-43.11, -63.39) * mm});
            skLineSegment(sketch, "E20.6.39.0", {"start": v(-50.17, -58.75) * mm, "end": v(-41.06, -61.45) * mm});
            skLineSegment(sketch, "E20.9.39.0", {"start": v(-41.24, -61.72) * mm, "end": v(-46.59, -60.54) * mm});
            skLineSegment(sketch, "E20.12.39.0", {"start": v(-41.06, -61.45) * mm, "end": v(-41.24, -61.72) * mm});
            skLineSegment(sketch, "E20.1.40.0", {"start": v(-38.88, -66.07) * mm, "end": v(-46.22, -61.9) * mm});
            skLineSegment(sketch, "E20.3.40.0", {"start": v(-42.53, -63.45) * mm, "end": v(-38.88, -66.07) * mm});
            skLineSegment(sketch, "E20.6.40.0", {"start": v(-46.22, -61.9) * mm, "end": v(-36.95, -64) * mm});
            skLineSegment(sketch, "E20.9.40.0", {"start": v(-37.12, -64.29) * mm, "end": v(-42.53, -63.45) * mm});
            skLineSegment(sketch, "E20.12.40.0", {"start": v(-36.95, -64) * mm, "end": v(-37.12, -64.29) * mm});
            skLineSegment(sketch, "E20.1.41.0", {"start": v(-34.47, -68.47) * mm, "end": v(-42.07, -64.8) * mm});
            skLineSegment(sketch, "E20.3.41.0", {"start": v(-38.29, -66.1) * mm, "end": v(-34.47, -68.47) * mm});
            skLineSegment(sketch, "E20.6.41.0", {"start": v(-42.07, -64.8) * mm, "end": v(-32.69, -66.28) * mm});
            skLineSegment(sketch, "E20.9.41.0", {"start": v(-32.83, -66.58) * mm, "end": v(-38.29, -66.1) * mm});
            skLineSegment(sketch, "E20.12.41.0", {"start": v(-32.69, -66.28) * mm, "end": v(-32.83, -66.58) * mm});
            skLineSegment(sketch, "E20.1.42.0", {"start": v(-29.92, -70.58) * mm, "end": v(-37.74, -67.4) * mm});
            skLineSegment(sketch, "E20.3.42.0", {"start": v(-33.88, -68.46) * mm, "end": v(-29.92, -70.58) * mm});
            skLineSegment(sketch, "E20.6.42.0", {"start": v(-37.74, -67.4) * mm, "end": v(-28.28, -68.28) * mm});
            skLineSegment(sketch, "E20.9.42.0", {"start": v(-28.4, -68.58) * mm, "end": v(-33.88, -68.46) * mm});
            skLineSegment(sketch, "E20.12.42.0", {"start": v(-28.28, -68.28) * mm, "end": v(-28.4, -68.58) * mm});
            skLineSegment(sketch, "E20.1.43.0", {"start": v(-25.24, -72.38) * mm, "end": v(-33.25, -69.73) * mm});
            skLineSegment(sketch, "E20.3.43.0", {"start": v(-29.33, -70.53) * mm, "end": v(-25.24, -72.38) * mm});
            skLineSegment(sketch, "E20.6.43.0", {"start": v(-33.25, -69.73) * mm, "end": v(-23.75, -69.98) * mm});
            skLineSegment(sketch, "E20.9.43.0", {"start": v(-23.86, -70.3) * mm, "end": v(-29.33, -70.53) * mm});
            skLineSegment(sketch, "E20.12.43.0", {"start": v(-23.75, -69.98) * mm, "end": v(-23.86, -70.3) * mm});
            skLineSegment(sketch, "E20.1.44.0", {"start": v(-20.45, -73.88) * mm, "end": v(-28.62, -71.75) * mm});
            skLineSegment(sketch, "E20.3.44.0", {"start": v(-24.66, -72.3) * mm, "end": v(-20.45, -73.88) * mm});
            skLineSegment(sketch, "E20.6.44.0", {"start": v(-28.62, -71.75) * mm, "end": v(-19.13, -71.38) * mm});
            skLineSegment(sketch, "E20.9.44.0", {"start": v(-19.21, -71.7) * mm, "end": v(-24.66, -72.3) * mm});
            skLineSegment(sketch, "E20.12.44.0", {"start": v(-19.13, -71.38) * mm, "end": v(-19.21, -71.7) * mm});
            skLineSegment(sketch, "E20.1.45.0", {"start": v(-15.58, -75.06) * mm, "end": v(-23.87, -73.47) * mm});
            skLineSegment(sketch, "E20.3.45.0", {"start": v(-19.88, -73.76) * mm, "end": v(-15.58, -75.06) * mm});
            skLineSegment(sketch, "E20.6.45.0", {"start": v(-23.87, -73.47) * mm, "end": v(-14.42, -72.48) * mm});
            skLineSegment(sketch, "E20.9.45.0", {"start": v(-14.48, -72.8) * mm, "end": v(-19.88, -73.76) * mm});
            skLineSegment(sketch, "E20.12.45.0", {"start": v(-14.42, -72.48) * mm, "end": v(-14.48, -72.8) * mm});
            skLineSegment(sketch, "E20.1.46.0", {"start": v(-10.63, -75.92) * mm, "end": v(-19, -74.88) * mm});
            skLineSegment(sketch, "E20.3.46.0", {"start": v(-15, -74.9) * mm, "end": v(-10.63, -75.92) * mm});
            skLineSegment(sketch, "E20.6.46.0", {"start": v(-19, -74.88) * mm, "end": v(-9.65, -73.27) * mm});
            skLineSegment(sketch, "E20.9.46.0", {"start": v(-9.69, -73.6) * mm, "end": v(-15, -74.9) * mm});
            skLineSegment(sketch, "E20.12.46.0", {"start": v(-9.65, -73.27) * mm, "end": v(-9.69, -73.6) * mm});
            skLineSegment(sketch, "E20.1.47.0", {"start": v(-5.64, -76.45) * mm, "end": v(-14.07, -75.96) * mm});
            skLineSegment(sketch, "E20.3.47.0", {"start": v(-10.08, -75.72) * mm, "end": v(-5.64, -76.45) * mm});
            skLineSegment(sketch, "E20.6.47.0", {"start": v(-14.07, -75.96) * mm, "end": v(-4.83, -73.74) * mm});
            skLineSegment(sketch, "E20.9.47.0", {"start": v(-4.85, -74.07) * mm, "end": v(-10.08, -75.72) * mm});
            skLineSegment(sketch, "E20.12.47.0", {"start": v(-4.83, -73.74) * mm, "end": v(-4.85, -74.07) * mm});
            skLineSegment(sketch, "E20.1.48.0", {"start": v(-0.63, -76.66) * mm, "end": v(-9.07, -76.72) * mm});
            skLineSegment(sketch, "E20.3.48.0", {"start": v(-5.1, -76.22) * mm, "end": v(-0.63, -76.66) * mm});
            skLineSegment(sketch, "E20.6.48.0", {"start": v(-9.07, -76.72) * mm, "end": v(0, -73.9) * mm});
            skLineSegment(sketch, "E20.9.48.0", {"start": v(0, -74.23) * mm, "end": v(-5.1, -76.22) * mm});
            skLineSegment(sketch, "E20.12.48.0", {"start": v(0, -73.9) * mm, "end": v(0, -74.23) * mm});
            skLineSegment(sketch, "E20.1.49.0", {"start": v(4.38, -76.53) * mm, "end": v(-4.04, -77.15) * mm});
            skLineSegment(sketch, "E20.3.49.0", {"start": v(-0.1, -76.39) * mm, "end": v(4.38, -76.53) * mm});
            skLineSegment(sketch, "E20.6.49.0", {"start": v(-4.04, -77.15) * mm, "end": v(4.83, -73.74) * mm});
            skLineSegment(sketch, "E20.9.49.0", {"start": v(4.85, -74.07) * mm, "end": v(-0.1, -76.39) * mm});
            skLineSegment(sketch, "E20.12.49.0", {"start": v(4.83, -73.74) * mm, "end": v(4.85, -74.07) * mm});
            skLineSegment(sketch, "E20.1.50.0", {"start": v(9.38, -76.08) * mm, "end": v(1.02, -77.24) * mm});
            skLineSegment(sketch, "E20.3.50.0", {"start": v(4.89, -76.23) * mm, "end": v(9.38, -76.08) * mm});
            skLineSegment(sketch, "E20.6.50.0", {"start": v(1.02, -77.24) * mm, "end": v(9.65, -73.27) * mm});
            skLineSegment(sketch, "E20.9.50.0", {"start": v(9.69, -73.6) * mm, "end": v(4.89, -76.23) * mm});
            skLineSegment(sketch, "E20.12.50.0", {"start": v(9.65, -73.27) * mm, "end": v(9.69, -73.6) * mm});
            skLineSegment(sketch, "E20.1.51.0", {"start": v(14.33, -75.3) * mm, "end": v(6.07, -77.01) * mm});
            skLineSegment(sketch, "E20.3.51.0", {"start": v(9.86, -75.75) * mm, "end": v(14.33, -75.3) * mm});
            skLineSegment(sketch, "E20.6.51.0", {"start": v(6.07, -77.01) * mm, "end": v(14.42, -72.48) * mm});
            skLineSegment(sketch, "E20.9.51.0", {"start": v(14.48, -72.8) * mm, "end": v(9.86, -75.75) * mm});
            skLineSegment(sketch, "E20.12.51.0", {"start": v(14.42, -72.48) * mm, "end": v(14.48, -72.8) * mm});
            skLineSegment(sketch, "E20.1.52.0", {"start": v(19.23, -74.2) * mm, "end": v(11.1, -76.45) * mm});
            skLineSegment(sketch, "E20.3.52.0", {"start": v(14.8, -74.94) * mm, "end": v(19.23, -74.2) * mm});
            skLineSegment(sketch, "E20.6.52.0", {"start": v(11.1, -76.45) * mm, "end": v(19.13, -71.38) * mm});
            skLineSegment(sketch, "E20.9.52.0", {"start": v(19.21, -71.7) * mm, "end": v(14.8, -74.94) * mm});
            skLineSegment(sketch, "E20.12.52.0", {"start": v(19.13, -71.38) * mm, "end": v(19.21, -71.7) * mm});
            skLineSegment(sketch, "E20.1.53.0", {"start": v(24.04, -72.8) * mm, "end": v(16.07, -75.56) * mm});
            skLineSegment(sketch, "E20.3.53.0", {"start": v(19.67, -73.81) * mm, "end": v(24.04, -72.8) * mm});
            skLineSegment(sketch, "E20.6.53.0", {"start": v(16.07, -75.56) * mm, "end": v(23.75, -69.98) * mm});
            skLineSegment(sketch, "E20.9.53.0", {"start": v(23.86, -70.3) * mm, "end": v(19.67, -73.81) * mm});
            skLineSegment(sketch, "E20.12.53.0", {"start": v(23.75, -69.98) * mm, "end": v(23.86, -70.3) * mm});
            skLineSegment(sketch, "E20.1.54.0", {"start": v(28.75, -71.06) * mm, "end": v(20.97, -74.35) * mm});
            skLineSegment(sketch, "E20.3.54.0", {"start": v(24.45, -72.37) * mm, "end": v(28.75, -71.06) * mm});
            skLineSegment(sketch, "E20.6.54.0", {"start": v(20.97, -74.35) * mm, "end": v(28.28, -68.28) * mm});
            skLineSegment(sketch, "E20.9.54.0", {"start": v(28.4, -68.58) * mm, "end": v(24.45, -72.37) * mm});
            skLineSegment(sketch, "E20.12.54.0", {"start": v(28.28, -68.28) * mm, "end": v(28.4, -68.58) * mm});
            skLineSegment(sketch, "E20.1.55.0", {"start": v(33.34, -69.03) * mm, "end": v(25.8, -72.82) * mm});
            skLineSegment(sketch, "E20.3.55.0", {"start": v(29.13, -70.61) * mm, "end": v(33.34, -69.03) * mm});
            skLineSegment(sketch, "E20.6.55.0", {"start": v(25.8, -72.82) * mm, "end": v(32.69, -66.28) * mm});
            skLineSegment(sketch, "E20.9.55.0", {"start": v(32.83, -66.58) * mm, "end": v(29.13, -70.61) * mm});
            skLineSegment(sketch, "E20.12.55.0", {"start": v(32.69, -66.28) * mm, "end": v(32.83, -66.58) * mm});
            skLineSegment(sketch, "E20.1.56.0", {"start": v(37.78, -66.7) * mm, "end": v(30.5, -70.97) * mm});
            skLineSegment(sketch, "E20.3.56.0", {"start": v(33.69, -68.56) * mm, "end": v(37.78, -66.7) * mm});
            skLineSegment(sketch, "E20.6.56.0", {"start": v(30.5, -70.97) * mm, "end": v(36.95, -64) * mm});
            skLineSegment(sketch, "E20.9.56.0", {"start": v(37.12, -64.29) * mm, "end": v(33.69, -68.56) * mm});
            skLineSegment(sketch, "E20.12.56.0", {"start": v(36.95, -64) * mm, "end": v(37.12, -64.29) * mm});
            skLineSegment(sketch, "E20.1.57.0", {"start": v(42.06, -64.09) * mm, "end": v(35.08, -68.83) * mm});
            skLineSegment(sketch, "E20.3.57.0", {"start": v(38.1, -66.2) * mm, "end": v(42.06, -64.09) * mm});
            skLineSegment(sketch, "E20.6.57.0", {"start": v(35.08, -68.83) * mm, "end": v(41.06, -61.45) * mm});
            skLineSegment(sketch, "E20.9.57.0", {"start": v(41.24, -61.72) * mm, "end": v(38.1, -66.2) * mm});
            skLineSegment(sketch, "E20.12.57.0", {"start": v(41.06, -61.45) * mm, "end": v(41.24, -61.72) * mm});
            skLineSegment(sketch, "E20.1.58.0", {"start": v(46.16, -61.2) * mm, "end": v(39.5, -66.39) * mm});
            skLineSegment(sketch, "E20.3.58.0", {"start": v(42.35, -63.57) * mm, "end": v(46.16, -61.2) * mm});
            skLineSegment(sketch, "E20.6.58.0", {"start": v(39.5, -66.39) * mm, "end": v(44.99, -58.63) * mm});
            skLineSegment(sketch, "E20.9.58.0", {"start": v(45.19, -58.9) * mm, "end": v(42.35, -63.57) * mm});
            skLineSegment(sketch, "E20.12.58.0", {"start": v(44.99, -58.63) * mm, "end": v(45.19, -58.9) * mm});
            skLineSegment(sketch, "E20.1.59.0", {"start": v(50.07, -58.05) * mm, "end": v(43.76, -63.66) * mm});
            skLineSegment(sketch, "E20.3.59.0", {"start": v(46.42, -60.67) * mm, "end": v(50.07, -58.05) * mm});
            skLineSegment(sketch, "E20.6.59.0", {"start": v(43.76, -63.66) * mm, "end": v(48.73, -55.56) * mm});
            skLineSegment(sketch, "E20.9.59.0", {"start": v(48.94, -55.81) * mm, "end": v(46.42, -60.67) * mm});
            skLineSegment(sketch, "E20.12.59.0", {"start": v(48.73, -55.56) * mm, "end": v(48.94, -55.81) * mm});
            skLineSegment(sketch, "E20.1.60.0", {"start": v(53.76, -54.65) * mm, "end": v(47.83, -60.66) * mm});
            skLineSegment(sketch, "E20.3.60.0", {"start": v(50.28, -57.5) * mm, "end": v(53.76, -54.65) * mm});
            skLineSegment(sketch, "E20.6.60.0", {"start": v(47.83, -60.66) * mm, "end": v(52.26, -52.26) * mm});
            skLineSegment(sketch, "E20.9.60.0", {"start": v(52.49, -52.49) * mm, "end": v(50.28, -57.5) * mm});
            skLineSegment(sketch, "E20.12.60.0", {"start": v(52.26, -52.26) * mm, "end": v(52.49, -52.49) * mm});
            skLineSegment(sketch, "E20.1.61.0", {"start": v(57.22, -51.02) * mm, "end": v(51.7, -57.4) * mm});
            skLineSegment(sketch, "E20.3.61.0", {"start": v(53.94, -54.1) * mm, "end": v(57.22, -51.02) * mm});
            skLineSegment(sketch, "E20.6.61.0", {"start": v(51.7, -57.4) * mm, "end": v(55.56, -48.73) * mm});
            skLineSegment(sketch, "E20.9.61.0", {"start": v(55.81, -48.94) * mm, "end": v(53.94, -54.1) * mm});
            skLineSegment(sketch, "E20.12.61.0", {"start": v(55.56, -48.73) * mm, "end": v(55.81, -48.94) * mm});
            skLineSegment(sketch, "E20.1.62.0", {"start": v(60.43, -47.17) * mm, "end": v(55.34, -53.9) * mm});
            skLineSegment(sketch, "E20.3.62.0", {"start": v(57.36, -50.45) * mm, "end": v(60.43, -47.17) * mm});
            skLineSegment(sketch, "E20.6.62.0", {"start": v(55.34, -53.9) * mm, "end": v(58.63, -44.99) * mm});
            skLineSegment(sketch, "E20.9.62.0", {"start": v(58.9, -45.19) * mm, "end": v(57.36, -50.45) * mm});
            skLineSegment(sketch, "E20.12.62.0", {"start": v(58.63, -44.99) * mm, "end": v(58.9, -45.19) * mm});
            skLineSegment(sketch, "E20.1.63.0", {"start": v(63.39, -43.11) * mm, "end": v(58.75, -50.17) * mm});
            skLineSegment(sketch, "E20.3.63.0", {"start": v(60.54, -46.59) * mm, "end": v(63.39, -43.11) * mm});
            skLineSegment(sketch, "E20.6.63.0", {"start": v(58.75, -50.17) * mm, "end": v(61.45, -41.06) * mm});
            skLineSegment(sketch, "E20.9.63.0", {"start": v(61.72, -41.24) * mm, "end": v(60.54, -46.59) * mm});
            skLineSegment(sketch, "E20.12.63.0", {"start": v(61.45, -41.06) * mm, "end": v(61.72, -41.24) * mm});
            skLineSegment(sketch, "E20.1.64.0", {"start": v(66.07, -38.88) * mm, "end": v(61.9, -46.22) * mm});
            skLineSegment(sketch, "E20.3.64.0", {"start": v(63.45, -42.53) * mm, "end": v(66.07, -38.88) * mm});
            skLineSegment(sketch, "E20.6.64.0", {"start": v(61.9, -46.22) * mm, "end": v(64, -36.95) * mm});
            skLineSegment(sketch, "E20.9.64.0", {"start": v(64.29, -37.12) * mm, "end": v(63.45, -42.53) * mm});
            skLineSegment(sketch, "E20.12.64.0", {"start": v(64, -36.95) * mm, "end": v(64.29, -37.12) * mm});
            skLineSegment(sketch, "E20.1.65.0", {"start": v(68.47, -34.47) * mm, "end": v(64.8, -42.07) * mm});
            skLineSegment(sketch, "E20.3.65.0", {"start": v(66.1, -38.29) * mm, "end": v(68.47, -34.47) * mm});
            skLineSegment(sketch, "E20.6.65.0", {"start": v(64.8, -42.07) * mm, "end": v(66.28, -32.69) * mm});
            skLineSegment(sketch, "E20.9.65.0", {"start": v(66.58, -32.83) * mm, "end": v(66.1, -38.29) * mm});
            skLineSegment(sketch, "E20.12.65.0", {"start": v(66.28, -32.69) * mm, "end": v(66.58, -32.83) * mm});
            skLineSegment(sketch, "E20.1.66.0", {"start": v(70.58, -29.92) * mm, "end": v(67.4, -37.74) * mm});
            skLineSegment(sketch, "E20.3.66.0", {"start": v(68.46, -33.88) * mm, "end": v(70.58, -29.92) * mm});
            skLineSegment(sketch, "E20.6.66.0", {"start": v(67.4, -37.74) * mm, "end": v(68.28, -28.28) * mm});
            skLineSegment(sketch, "E20.9.66.0", {"start": v(68.58, -28.4) * mm, "end": v(68.46, -33.88) * mm});
            skLineSegment(sketch, "E20.12.66.0", {"start": v(68.28, -28.28) * mm, "end": v(68.58, -28.4) * mm});
            skLineSegment(sketch, "E20.1.67.0", {"start": v(72.38, -25.24) * mm, "end": v(69.73, -33.25) * mm});
            skLineSegment(sketch, "E20.3.67.0", {"start": v(70.53, -29.33) * mm, "end": v(72.38, -25.24) * mm});
            skLineSegment(sketch, "E20.6.67.0", {"start": v(69.73, -33.25) * mm, "end": v(69.98, -23.75) * mm});
            skLineSegment(sketch, "E20.9.67.0", {"start": v(70.3, -23.86) * mm, "end": v(70.53, -29.33) * mm});
            skLineSegment(sketch, "E20.12.67.0", {"start": v(69.98, -23.75) * mm, "end": v(70.3, -23.86) * mm});
            skLineSegment(sketch, "E20.1.68.0", {"start": v(73.88, -20.45) * mm, "end": v(71.75, -28.62) * mm});
            skLineSegment(sketch, "E20.3.68.0", {"start": v(72.3, -24.66) * mm, "end": v(73.88, -20.45) * mm});
            skLineSegment(sketch, "E20.6.68.0", {"start": v(71.75, -28.62) * mm, "end": v(71.38, -19.13) * mm});
            skLineSegment(sketch, "E20.9.68.0", {"start": v(71.7, -19.21) * mm, "end": v(72.3, -24.66) * mm});
            skLineSegment(sketch, "E20.12.68.0", {"start": v(71.38, -19.13) * mm, "end": v(71.7, -19.21) * mm});
            skLineSegment(sketch, "E20.1.69.0", {"start": v(75.06, -15.58) * mm, "end": v(73.47, -23.87) * mm});
            skLineSegment(sketch, "E20.3.69.0", {"start": v(73.76, -19.88) * mm, "end": v(75.06, -15.58) * mm});
            skLineSegment(sketch, "E20.6.69.0", {"start": v(73.47, -23.87) * mm, "end": v(72.48, -14.42) * mm});
            skLineSegment(sketch, "E20.9.69.0", {"start": v(72.8, -14.48) * mm, "end": v(73.76, -19.88) * mm});
            skLineSegment(sketch, "E20.12.69.0", {"start": v(72.48, -14.42) * mm, "end": v(72.8, -14.48) * mm});
            skLineSegment(sketch, "E20.1.70.0", {"start": v(75.92, -10.63) * mm, "end": v(74.88, -19) * mm});
            skLineSegment(sketch, "E20.3.70.0", {"start": v(74.9, -15) * mm, "end": v(75.92, -10.63) * mm});
            skLineSegment(sketch, "E20.6.70.0", {"start": v(74.88, -19) * mm, "end": v(73.27, -9.65) * mm});
            skLineSegment(sketch, "E20.9.70.0", {"start": v(73.6, -9.69) * mm, "end": v(74.9, -15) * mm});
            skLineSegment(sketch, "E20.12.70.0", {"start": v(73.27, -9.65) * mm, "end": v(73.6, -9.69) * mm});
            skLineSegment(sketch, "E20.1.71.0", {"start": v(76.45, -5.64) * mm, "end": v(75.96, -14.07) * mm});
            skLineSegment(sketch, "E20.3.71.0", {"start": v(75.72, -10.08) * mm, "end": v(76.45, -5.64) * mm});
            skLineSegment(sketch, "E20.6.71.0", {"start": v(75.96, -14.07) * mm, "end": v(73.74, -4.83) * mm});
            skLineSegment(sketch, "E20.9.71.0", {"start": v(74.07, -4.85) * mm, "end": v(75.72, -10.08) * mm});
            skLineSegment(sketch, "E20.12.71.0", {"start": v(73.74, -4.83) * mm, "end": v(74.07, -4.85) * mm});
            skLineSegment(sketch, "E20.1.72.0", {"start": v(76.66, -0.63) * mm, "end": v(76.72, -9.07) * mm});
            skLineSegment(sketch, "E20.3.72.0", {"start": v(76.22, -5.1) * mm, "end": v(76.66, -0.63) * mm});
            skLineSegment(sketch, "E20.6.72.0", {"start": v(76.72, -9.07) * mm, "end": v(73.9, 0) * mm});
            skLineSegment(sketch, "E20.9.72.0", {"start": v(74.23, 0) * mm, "end": v(76.22, -5.1) * mm});
            skLineSegment(sketch, "E20.12.72.0", {"start": v(73.9, 0) * mm, "end": v(74.23, 0) * mm});
            skLineSegment(sketch, "E20.1.73.0", {"start": v(76.53, 4.38) * mm, "end": v(77.15, -4.04) * mm});
            skLineSegment(sketch, "E20.3.73.0", {"start": v(76.39, -0.1) * mm, "end": v(76.53, 4.38) * mm});
            skLineSegment(sketch, "E20.6.73.0", {"start": v(77.15, -4.04) * mm, "end": v(73.74, 4.83) * mm});
            skLineSegment(sketch, "E20.9.73.0", {"start": v(74.07, 4.85) * mm, "end": v(76.39, -0.1) * mm});
            skLineSegment(sketch, "E20.12.73.0", {"start": v(73.74, 4.83) * mm, "end": v(74.07, 4.85) * mm});
            skLineSegment(sketch, "E20.1.74.0", {"start": v(76.08, 9.38) * mm, "end": v(77.24, 1.02) * mm});
            skLineSegment(sketch, "E20.3.74.0", {"start": v(76.23, 4.89) * mm, "end": v(76.08, 9.38) * mm});
            skLineSegment(sketch, "E20.6.74.0", {"start": v(77.24, 1.02) * mm, "end": v(73.27, 9.65) * mm});
            skLineSegment(sketch, "E20.9.74.0", {"start": v(73.6, 9.69) * mm, "end": v(76.23, 4.89) * mm});
            skLineSegment(sketch, "E20.12.74.0", {"start": v(73.27, 9.65) * mm, "end": v(73.6, 9.69) * mm});
            skLineSegment(sketch, "E20.1.75.0", {"start": v(75.3, 14.33) * mm, "end": v(77.01, 6.07) * mm});
            skLineSegment(sketch, "E20.3.75.0", {"start": v(75.75, 9.86) * mm, "end": v(75.3, 14.33) * mm});
            skLineSegment(sketch, "E20.6.75.0", {"start": v(77.01, 6.07) * mm, "end": v(72.48, 14.42) * mm});
            skLineSegment(sketch, "E20.9.75.0", {"start": v(72.8, 14.48) * mm, "end": v(75.75, 9.86) * mm});
            skLineSegment(sketch, "E20.12.75.0", {"start": v(72.48, 14.42) * mm, "end": v(72.8, 14.48) * mm});
            skLineSegment(sketch, "E20.1.76.0", {"start": v(74.2, 19.23) * mm, "end": v(76.45, 11.1) * mm});
            skLineSegment(sketch, "E20.3.76.0", {"start": v(74.94, 14.8) * mm, "end": v(74.2, 19.23) * mm});
            skLineSegment(sketch, "E20.6.76.0", {"start": v(76.45, 11.1) * mm, "end": v(71.38, 19.13) * mm});
            skLineSegment(sketch, "E20.9.76.0", {"start": v(71.7, 19.21) * mm, "end": v(74.94, 14.8) * mm});
            skLineSegment(sketch, "E20.12.76.0", {"start": v(71.38, 19.13) * mm, "end": v(71.7, 19.21) * mm});
            skLineSegment(sketch, "E20.1.77.0", {"start": v(72.8, 24.04) * mm, "end": v(75.56, 16.07) * mm});
            skLineSegment(sketch, "E20.3.77.0", {"start": v(73.81, 19.67) * mm, "end": v(72.8, 24.04) * mm});
            skLineSegment(sketch, "E20.6.77.0", {"start": v(75.56, 16.07) * mm, "end": v(69.98, 23.75) * mm});
            skLineSegment(sketch, "E20.9.77.0", {"start": v(70.3, 23.86) * mm, "end": v(73.81, 19.67) * mm});
            skLineSegment(sketch, "E20.12.77.0", {"start": v(69.98, 23.75) * mm, "end": v(70.3, 23.86) * mm});
            skLineSegment(sketch, "E20.1.78.0", {"start": v(71.06, 28.75) * mm, "end": v(74.35, 20.97) * mm});
            skLineSegment(sketch, "E20.3.78.0", {"start": v(72.37, 24.45) * mm, "end": v(71.06, 28.75) * mm});
            skLineSegment(sketch, "E20.6.78.0", {"start": v(74.35, 20.97) * mm, "end": v(68.28, 28.28) * mm});
            skLineSegment(sketch, "E20.9.78.0", {"start": v(68.58, 28.4) * mm, "end": v(72.37, 24.45) * mm});
            skLineSegment(sketch, "E20.12.78.0", {"start": v(68.28, 28.28) * mm, "end": v(68.58, 28.4) * mm});
            skLineSegment(sketch, "E20.1.79.0", {"start": v(69.03, 33.34) * mm, "end": v(72.82, 25.8) * mm});
            skLineSegment(sketch, "E20.3.79.0", {"start": v(70.61, 29.13) * mm, "end": v(69.03, 33.34) * mm});
            skLineSegment(sketch, "E20.6.79.0", {"start": v(72.82, 25.8) * mm, "end": v(66.28, 32.69) * mm});
            skLineSegment(sketch, "E20.9.79.0", {"start": v(66.58, 32.83) * mm, "end": v(70.61, 29.13) * mm});
            skLineSegment(sketch, "E20.12.79.0", {"start": v(66.28, 32.69) * mm, "end": v(66.58, 32.83) * mm});
            skLineSegment(sketch, "E20.1.80.0", {"start": v(66.7, 37.78) * mm, "end": v(70.97, 30.5) * mm});
            skLineSegment(sketch, "E20.3.80.0", {"start": v(68.56, 33.69) * mm, "end": v(66.7, 37.78) * mm});
            skLineSegment(sketch, "E20.6.80.0", {"start": v(70.97, 30.5) * mm, "end": v(64, 36.95) * mm});
            skLineSegment(sketch, "E20.9.80.0", {"start": v(64.29, 37.12) * mm, "end": v(68.56, 33.69) * mm});
            skLineSegment(sketch, "E20.12.80.0", {"start": v(64, 36.95) * mm, "end": v(64.29, 37.12) * mm});
            skLineSegment(sketch, "E20.1.81.0", {"start": v(64.09, 42.06) * mm, "end": v(68.83, 35.08) * mm});
            skLineSegment(sketch, "E20.3.81.0", {"start": v(66.2, 38.1) * mm, "end": v(64.09, 42.06) * mm});
            skLineSegment(sketch, "E20.6.81.0", {"start": v(68.83, 35.08) * mm, "end": v(61.45, 41.06) * mm});
            skLineSegment(sketch, "E20.9.81.0", {"start": v(61.72, 41.24) * mm, "end": v(66.2, 38.1) * mm});
            skLineSegment(sketch, "E20.12.81.0", {"start": v(61.45, 41.06) * mm, "end": v(61.72, 41.24) * mm});
            skLineSegment(sketch, "E20.1.82.0", {"start": v(61.2, 46.16) * mm, "end": v(66.39, 39.5) * mm});
            skLineSegment(sketch, "E20.3.82.0", {"start": v(63.57, 42.35) * mm, "end": v(61.2, 46.16) * mm});
            skLineSegment(sketch, "E20.6.82.0", {"start": v(66.39, 39.5) * mm, "end": v(58.63, 44.99) * mm});
            skLineSegment(sketch, "E20.9.82.0", {"start": v(58.9, 45.19) * mm, "end": v(63.57, 42.35) * mm});
            skLineSegment(sketch, "E20.12.82.0", {"start": v(58.63, 44.99) * mm, "end": v(58.9, 45.19) * mm});
            skLineSegment(sketch, "E20.1.83.0", {"start": v(58.05, 50.07) * mm, "end": v(63.66, 43.76) * mm});
            skLineSegment(sketch, "E20.3.83.0", {"start": v(60.67, 46.42) * mm, "end": v(58.05, 50.07) * mm});
            skLineSegment(sketch, "E20.6.83.0", {"start": v(63.66, 43.76) * mm, "end": v(55.56, 48.73) * mm});
            skLineSegment(sketch, "E20.9.83.0", {"start": v(55.81, 48.94) * mm, "end": v(60.67, 46.42) * mm});
            skLineSegment(sketch, "E20.12.83.0", {"start": v(55.56, 48.73) * mm, "end": v(55.81, 48.94) * mm});
            skLineSegment(sketch, "E20.1.84.0", {"start": v(54.65, 53.76) * mm, "end": v(60.66, 47.83) * mm});
            skLineSegment(sketch, "E20.3.84.0", {"start": v(57.5, 50.28) * mm, "end": v(54.65, 53.76) * mm});
            skLineSegment(sketch, "E20.6.84.0", {"start": v(60.66, 47.83) * mm, "end": v(52.26, 52.26) * mm});
            skLineSegment(sketch, "E20.9.84.0", {"start": v(52.49, 52.49) * mm, "end": v(57.5, 50.28) * mm});
            skLineSegment(sketch, "E20.12.84.0", {"start": v(52.26, 52.26) * mm, "end": v(52.49, 52.49) * mm});
            skLineSegment(sketch, "E20.1.85.0", {"start": v(51.02, 57.22) * mm, "end": v(57.4, 51.7) * mm});
            skLineSegment(sketch, "E20.3.85.0", {"start": v(54.1, 53.94) * mm, "end": v(51.02, 57.22) * mm});
            skLineSegment(sketch, "E20.6.85.0", {"start": v(57.4, 51.7) * mm, "end": v(48.73, 55.56) * mm});
            skLineSegment(sketch, "E20.9.85.0", {"start": v(48.94, 55.81) * mm, "end": v(54.1, 53.94) * mm});
            skLineSegment(sketch, "E20.12.85.0", {"start": v(48.73, 55.56) * mm, "end": v(48.94, 55.81) * mm});
            skLineSegment(sketch, "E20.1.86.0", {"start": v(47.17, 60.43) * mm, "end": v(53.9, 55.34) * mm});
            skLineSegment(sketch, "E20.3.86.0", {"start": v(50.45, 57.36) * mm, "end": v(47.17, 60.43) * mm});
            skLineSegment(sketch, "E20.6.86.0", {"start": v(53.9, 55.34) * mm, "end": v(44.99, 58.63) * mm});
            skLineSegment(sketch, "E20.9.86.0", {"start": v(45.19, 58.9) * mm, "end": v(50.45, 57.36) * mm});
            skLineSegment(sketch, "E20.12.86.0", {"start": v(44.99, 58.63) * mm, "end": v(45.19, 58.9) * mm});
            skLineSegment(sketch, "E20.1.87.0", {"start": v(43.11, 63.39) * mm, "end": v(50.17, 58.75) * mm});
            skLineSegment(sketch, "E20.3.87.0", {"start": v(46.59, 60.54) * mm, "end": v(43.11, 63.39) * mm});
            skLineSegment(sketch, "E20.6.87.0", {"start": v(50.17, 58.75) * mm, "end": v(41.06, 61.45) * mm});
            skLineSegment(sketch, "E20.9.87.0", {"start": v(41.24, 61.72) * mm, "end": v(46.59, 60.54) * mm});
            skLineSegment(sketch, "E20.12.87.0", {"start": v(41.06, 61.45) * mm, "end": v(41.24, 61.72) * mm});
            skLineSegment(sketch, "E20.1.88.0", {"start": v(38.88, 66.07) * mm, "end": v(46.22, 61.9) * mm});
            skLineSegment(sketch, "E20.3.88.0", {"start": v(42.53, 63.45) * mm, "end": v(38.88, 66.07) * mm});
            skLineSegment(sketch, "E20.6.88.0", {"start": v(46.22, 61.9) * mm, "end": v(36.95, 64) * mm});
            skLineSegment(sketch, "E20.9.88.0", {"start": v(37.12, 64.29) * mm, "end": v(42.53, 63.45) * mm});
            skLineSegment(sketch, "E20.12.88.0", {"start": v(36.95, 64) * mm, "end": v(37.12, 64.29) * mm});
            skLineSegment(sketch, "E20.1.89.0", {"start": v(34.47, 68.47) * mm, "end": v(42.07, 64.8) * mm});
            skLineSegment(sketch, "E20.3.89.0", {"start": v(38.29, 66.1) * mm, "end": v(34.47, 68.47) * mm});
            skLineSegment(sketch, "E20.6.89.0", {"start": v(42.07, 64.8) * mm, "end": v(32.69, 66.28) * mm});
            skLineSegment(sketch, "E20.9.89.0", {"start": v(32.83, 66.58) * mm, "end": v(38.29, 66.1) * mm});
            skLineSegment(sketch, "E20.12.89.0", {"start": v(32.69, 66.28) * mm, "end": v(32.83, 66.58) * mm});
            skLineSegment(sketch, "E20.1.90.0", {"start": v(29.92, 70.58) * mm, "end": v(37.74, 67.4) * mm});
            skLineSegment(sketch, "E20.3.90.0", {"start": v(33.88, 68.46) * mm, "end": v(29.92, 70.58) * mm});
            skLineSegment(sketch, "E20.6.90.0", {"start": v(37.74, 67.4) * mm, "end": v(28.28, 68.28) * mm});
            skLineSegment(sketch, "E20.9.90.0", {"start": v(28.4, 68.58) * mm, "end": v(33.88, 68.46) * mm});
            skLineSegment(sketch, "E20.12.90.0", {"start": v(28.28, 68.28) * mm, "end": v(28.4, 68.58) * mm});
            skLineSegment(sketch, "E20.1.91.0", {"start": v(25.24, 72.38) * mm, "end": v(33.25, 69.73) * mm});
            skLineSegment(sketch, "E20.3.91.0", {"start": v(29.33, 70.53) * mm, "end": v(25.24, 72.38) * mm});
            skLineSegment(sketch, "E20.6.91.0", {"start": v(33.25, 69.73) * mm, "end": v(23.75, 69.98) * mm});
            skLineSegment(sketch, "E20.9.91.0", {"start": v(23.86, 70.3) * mm, "end": v(29.33, 70.53) * mm});
            skLineSegment(sketch, "E20.12.91.0", {"start": v(23.75, 69.98) * mm, "end": v(23.86, 70.3) * mm});
            skLineSegment(sketch, "E20.1.92.0", {"start": v(20.45, 73.88) * mm, "end": v(28.62, 71.75) * mm});
            skLineSegment(sketch, "E20.3.92.0", {"start": v(24.66, 72.3) * mm, "end": v(20.45, 73.88) * mm});
            skLineSegment(sketch, "E20.6.92.0", {"start": v(28.62, 71.75) * mm, "end": v(19.13, 71.38) * mm});
            skLineSegment(sketch, "E20.9.92.0", {"start": v(19.21, 71.7) * mm, "end": v(24.66, 72.3) * mm});
            skLineSegment(sketch, "E20.12.92.0", {"start": v(19.13, 71.38) * mm, "end": v(19.21, 71.7) * mm});
            skLineSegment(sketch, "E20.1.93.0", {"start": v(15.58, 75.06) * mm, "end": v(23.87, 73.47) * mm});
            skLineSegment(sketch, "E20.3.93.0", {"start": v(19.88, 73.76) * mm, "end": v(15.58, 75.06) * mm});
            skLineSegment(sketch, "E20.6.93.0", {"start": v(23.87, 73.47) * mm, "end": v(14.42, 72.48) * mm});
            skLineSegment(sketch, "E20.9.93.0", {"start": v(14.48, 72.8) * mm, "end": v(19.88, 73.76) * mm});
            skLineSegment(sketch, "E20.12.93.0", {"start": v(14.42, 72.48) * mm, "end": v(14.48, 72.8) * mm});
            skLineSegment(sketch, "E20.1.94.0", {"start": v(10.63, 75.92) * mm, "end": v(19, 74.88) * mm});
            skLineSegment(sketch, "E20.3.94.0", {"start": v(15, 74.9) * mm, "end": v(10.63, 75.92) * mm});
            skLineSegment(sketch, "E20.6.94.0", {"start": v(19, 74.88) * mm, "end": v(9.65, 73.27) * mm});
            skLineSegment(sketch, "E20.9.94.0", {"start": v(9.69, 73.6) * mm, "end": v(15, 74.9) * mm});
            skLineSegment(sketch, "E20.12.94.0", {"start": v(9.65, 73.27) * mm, "end": v(9.69, 73.6) * mm});
            skLineSegment(sketch, "E20.1.95.0", {"start": v(5.64, 76.45) * mm, "end": v(14.07, 75.96) * mm});
            skLineSegment(sketch, "E20.3.95.0", {"start": v(10.08, 75.72) * mm, "end": v(5.64, 76.45) * mm});
            skLineSegment(sketch, "E20.6.95.0", {"start": v(14.07, 75.96) * mm, "end": v(4.83, 73.74) * mm});
            skLineSegment(sketch, "E20.9.95.0", {"start": v(4.85, 74.07) * mm, "end": v(10.08, 75.72) * mm});
            skLineSegment(sketch, "E20.12.95.0", {"start": v(4.83, 73.74) * mm, "end": v(4.85, 74.07) * mm});
            skSolve(sketch);
        }
        {
            var Q0;
            Q0 = qSketchRegion(id + "F8", true);
            extrude(context, id + "F9", {"entities" : qUnion([Q0]), "operationType" : NewBodyOperationType.REMOVE, "oppositeDirection" : true, "depth" : 10.16 * mm});
        }
        {
            var Q0;
            {var subQ0=sQuery(id+"F0.wireOp",EDGE,"E1");Q0=makeQuery(id+"F5.boolean.opBoolean","SPLIT",FACE,{"disambiguationData":[TD([makeQuery(id+"F1.opExtrude","SWEPT_FACE",FACE,{"disambiguationData":[OSD([subQ0])]})])],"derivedFrom":makeQuery(id+"F1.opExtrude","CAP_FACE",FACE,{"disambiguationData":[OSD([sQuery(id+"F0.wireOp",EDGE,"E0"),subQ0])],"isStart":false})});}
            var sketch = newSketch(context, id + "F10", { "sketchPlane" : qUnion([Q0])});
            skLineSegment(sketch, "E21", {"start": v(-7.62, 65.26) * mm, "end": v(7.62, 65.26) * mm});
            skLineSegment(sketch, "E22", {"start": v(7.62, 65.26) * mm, "end": v(5.65, 62.45) * mm});
            skLineSegment(sketch, "E23", {"start": v(5.65, 62.45) * mm, "end": v(-5.65, 62.45) * mm});
            skLineSegment(sketch, "E24", {"start": v(-5.65, 62.45) * mm, "end": v(-7.62, 65.26) * mm});
            skLineSegment(sketch, "E25.1.0", {"start": v(-32.01, 57.38) * mm, "end": v(-17.93, 63.2) * mm});
            skLineSegment(sketch, "E25.1.1", {"start": v(-17.93, 63.2) * mm, "end": v(-18.68, 59.86) * mm});
            skLineSegment(sketch, "E25.1.2", {"start": v(-18.68, 59.86) * mm, "end": v(-29.12, 55.53) * mm});
            skLineSegment(sketch, "E25.1.3", {"start": v(-29.12, 55.53) * mm, "end": v(-32.01, 57.38) * mm});
            skLineSegment(sketch, "E25.2.0", {"start": v(-51.53, 40.76) * mm, "end": v(-40.76, 51.53) * mm});
            skLineSegment(sketch, "E25.2.1", {"start": v(-40.76, 51.53) * mm, "end": v(-40.16, 48.16) * mm});
            skLineSegment(sketch, "E25.2.2", {"start": v(-40.16, 48.16) * mm, "end": v(-48.16, 40.16) * mm});
            skLineSegment(sketch, "E25.2.3", {"start": v(-48.16, 40.16) * mm, "end": v(-51.53, 40.76) * mm});
            skLineSegment(sketch, "E25.3.0", {"start": v(-63.2, 17.93) * mm, "end": v(-57.38, 32.01) * mm});
            skLineSegment(sketch, "E25.3.1", {"start": v(-57.38, 32.01) * mm, "end": v(-55.53, 29.12) * mm});
            skLineSegment(sketch, "E25.3.2", {"start": v(-55.53, 29.12) * mm, "end": v(-59.86, 18.68) * mm});
            skLineSegment(sketch, "E25.3.3", {"start": v(-59.86, 18.68) * mm, "end": v(-63.2, 17.93) * mm});
            skLineSegment(sketch, "E25.4.0", {"start": v(-65.26, -7.62) * mm, "end": v(-65.26, 7.62) * mm});
            skLineSegment(sketch, "E25.4.1", {"start": v(-65.26, 7.62) * mm, "end": v(-62.45, 5.65) * mm});
            skLineSegment(sketch, "E25.4.2", {"start": v(-62.45, 5.65) * mm, "end": v(-62.45, -5.65) * mm});
            skLineSegment(sketch, "E25.4.3", {"start": v(-62.45, -5.65) * mm, "end": v(-65.26, -7.62) * mm});
            skLineSegment(sketch, "E25.5.0", {"start": v(-57.38, -32.01) * mm, "end": v(-63.2, -17.93) * mm});
            skLineSegment(sketch, "E25.5.1", {"start": v(-63.2, -17.93) * mm, "end": v(-59.86, -18.68) * mm});
            skLineSegment(sketch, "E25.5.2", {"start": v(-59.86, -18.68) * mm, "end": v(-55.53, -29.12) * mm});
            skLineSegment(sketch, "E25.5.3", {"start": v(-55.53, -29.12) * mm, "end": v(-57.38, -32.01) * mm});
            skLineSegment(sketch, "E25.6.0", {"start": v(-40.76, -51.53) * mm, "end": v(-51.53, -40.76) * mm});
            skLineSegment(sketch, "E25.6.1", {"start": v(-51.53, -40.76) * mm, "end": v(-48.16, -40.16) * mm});
            skLineSegment(sketch, "E25.6.2", {"start": v(-48.16, -40.16) * mm, "end": v(-40.16, -48.16) * mm});
            skLineSegment(sketch, "E25.6.3", {"start": v(-40.16, -48.16) * mm, "end": v(-40.76, -51.53) * mm});
            skLineSegment(sketch, "E25.7.0", {"start": v(-17.93, -63.2) * mm, "end": v(-32.01, -57.38) * mm});
            skLineSegment(sketch, "E25.7.1", {"start": v(-32.01, -57.38) * mm, "end": v(-29.12, -55.53) * mm});
            skLineSegment(sketch, "E25.7.2", {"start": v(-29.12, -55.53) * mm, "end": v(-18.68, -59.86) * mm});
            skLineSegment(sketch, "E25.7.3", {"start": v(-18.68, -59.86) * mm, "end": v(-17.93, -63.2) * mm});
            skLineSegment(sketch, "E25.8.0", {"start": v(7.62, -65.26) * mm, "end": v(-7.62, -65.26) * mm});
            skLineSegment(sketch, "E25.8.1", {"start": v(-7.62, -65.26) * mm, "end": v(-5.65, -62.45) * mm});
            skLineSegment(sketch, "E25.8.2", {"start": v(-5.65, -62.45) * mm, "end": v(5.65, -62.45) * mm});
            skLineSegment(sketch, "E25.8.3", {"start": v(5.65, -62.45) * mm, "end": v(7.62, -65.26) * mm});
            skLineSegment(sketch, "E25.9.0", {"start": v(32.01, -57.38) * mm, "end": v(17.93, -63.2) * mm});
            skLineSegment(sketch, "E25.9.1", {"start": v(17.93, -63.2) * mm, "end": v(18.68, -59.86) * mm});
            skLineSegment(sketch, "E25.9.2", {"start": v(18.68, -59.86) * mm, "end": v(29.12, -55.53) * mm});
            skLineSegment(sketch, "E25.9.3", {"start": v(29.12, -55.53) * mm, "end": v(32.01, -57.38) * mm});
            skLineSegment(sketch, "E25.10.0", {"start": v(51.53, -40.76) * mm, "end": v(40.76, -51.53) * mm});
            skLineSegment(sketch, "E25.10.1", {"start": v(40.76, -51.53) * mm, "end": v(40.16, -48.16) * mm});
            skLineSegment(sketch, "E25.10.2", {"start": v(40.16, -48.16) * mm, "end": v(48.16, -40.16) * mm});
            skLineSegment(sketch, "E25.10.3", {"start": v(48.16, -40.16) * mm, "end": v(51.53, -40.76) * mm});
            skLineSegment(sketch, "E25.11.0", {"start": v(63.2, -17.93) * mm, "end": v(57.38, -32.01) * mm});
            skLineSegment(sketch, "E25.11.1", {"start": v(57.38, -32.01) * mm, "end": v(55.53, -29.12) * mm});
            skLineSegment(sketch, "E25.11.2", {"start": v(55.53, -29.12) * mm, "end": v(59.86, -18.68) * mm});
            skLineSegment(sketch, "E25.11.3", {"start": v(59.86, -18.68) * mm, "end": v(63.2, -17.93) * mm});
            skLineSegment(sketch, "E25.12.0", {"start": v(65.26, 7.62) * mm, "end": v(65.26, -7.62) * mm});
            skLineSegment(sketch, "E25.12.1", {"start": v(65.26, -7.62) * mm, "end": v(62.45, -5.65) * mm});
            skLineSegment(sketch, "E25.12.2", {"start": v(62.45, -5.65) * mm, "end": v(62.45, 5.65) * mm});
            skLineSegment(sketch, "E25.12.3", {"start": v(62.45, 5.65) * mm, "end": v(65.26, 7.62) * mm});
            skLineSegment(sketch, "E25.13.0", {"start": v(57.38, 32.01) * mm, "end": v(63.2, 17.93) * mm});
            skLineSegment(sketch, "E25.13.1", {"start": v(63.2, 17.93) * mm, "end": v(59.86, 18.68) * mm});
            skLineSegment(sketch, "E25.13.2", {"start": v(59.86, 18.68) * mm, "end": v(55.53, 29.12) * mm});
            skLineSegment(sketch, "E25.13.3", {"start": v(55.53, 29.12) * mm, "end": v(57.38, 32.01) * mm});
            skLineSegment(sketch, "E25.14.0", {"start": v(40.76, 51.53) * mm, "end": v(51.53, 40.76) * mm});
            skLineSegment(sketch, "E25.14.1", {"start": v(51.53, 40.76) * mm, "end": v(48.16, 40.16) * mm});
            skLineSegment(sketch, "E25.14.2", {"start": v(48.16, 40.16) * mm, "end": v(40.16, 48.16) * mm});
            skLineSegment(sketch, "E25.14.3", {"start": v(40.16, 48.16) * mm, "end": v(40.76, 51.53) * mm});
            skLineSegment(sketch, "E25.15.0", {"start": v(17.93, 63.2) * mm, "end": v(32.01, 57.38) * mm});
            skLineSegment(sketch, "E25.15.1", {"start": v(32.01, 57.38) * mm, "end": v(29.12, 55.53) * mm});
            skLineSegment(sketch, "E25.15.2", {"start": v(29.12, 55.53) * mm, "end": v(18.68, 59.86) * mm});
            skLineSegment(sketch, "E25.15.3", {"start": v(18.68, 59.86) * mm, "end": v(17.93, 63.2) * mm});
            skPoint(sketch, "E25.center", {"position": v(0, 0) * mm});
            skSolve(sketch);
        }
        {
            var Q0;
            Q0 = qSketchRegion(id + "F10", true);
            extrude(context, id + "F11", {"entities" : qUnion([Q0]), "operationType" : NewBodyOperationType.REMOVE, "oppositeDirection" : true, "depth" : 1.02 * mm});
        }
        {
            var Q0;
            {var subQ0=sQuery(id+"F0.wireOp",EDGE,"E1");Q0=makeQuery(id+"F5.boolean.opBoolean","SPLIT",FACE,{"disambiguationData":[TD([makeQuery(id+"F1.opExtrude","SWEPT_FACE",FACE,{"disambiguationData":[OSD([subQ0])]})])],"derivedFrom":makeQuery(id+"F1.opExtrude","CAP_FACE",FACE,{"disambiguationData":[OSD([sQuery(id+"F0.wireOp",EDGE,"E0"),subQ0])],"isStart":true})});}
            var sketch = newSketch(context, id + "F12", { "sketchPlane" : qUnion([Q0])});
            skLineSegment(sketch, "E26", {"start": v(-7.62, 65.26) * mm, "end": v(7.62, 65.26) * mm});
            skLineSegment(sketch, "E27", {"start": v(7.62, 65.26) * mm, "end": v(5.65, 62.45) * mm});
            skLineSegment(sketch, "E28", {"start": v(5.65, 62.45) * mm, "end": v(-5.65, 62.45) * mm});
            skLineSegment(sketch, "E29", {"start": v(-5.65, 62.45) * mm, "end": v(-7.62, 65.26) * mm});
            skLineSegment(sketch, "E30.1.0", {"start": v(-32.01, 57.38) * mm, "end": v(-17.93, 63.2) * mm});
            skLineSegment(sketch, "E30.1.1", {"start": v(-17.93, 63.2) * mm, "end": v(-18.68, 59.86) * mm});
            skLineSegment(sketch, "E30.1.2", {"start": v(-18.68, 59.86) * mm, "end": v(-29.12, 55.53) * mm});
            skLineSegment(sketch, "E30.1.3", {"start": v(-29.12, 55.53) * mm, "end": v(-32.01, 57.38) * mm});
            skLineSegment(sketch, "E30.2.0", {"start": v(-51.53, 40.76) * mm, "end": v(-40.76, 51.53) * mm});
            skLineSegment(sketch, "E30.2.1", {"start": v(-40.76, 51.53) * mm, "end": v(-40.16, 48.16) * mm});
            skLineSegment(sketch, "E30.2.2", {"start": v(-40.16, 48.16) * mm, "end": v(-48.16, 40.16) * mm});
            skLineSegment(sketch, "E30.2.3", {"start": v(-48.16, 40.16) * mm, "end": v(-51.53, 40.76) * mm});
            skLineSegment(sketch, "E30.3.0", {"start": v(-63.2, 17.93) * mm, "end": v(-57.38, 32.01) * mm});
            skLineSegment(sketch, "E30.3.1", {"start": v(-57.38, 32.01) * mm, "end": v(-55.53, 29.12) * mm});
            skLineSegment(sketch, "E30.3.2", {"start": v(-55.53, 29.12) * mm, "end": v(-59.86, 18.68) * mm});
            skLineSegment(sketch, "E30.3.3", {"start": v(-59.86, 18.68) * mm, "end": v(-63.2, 17.93) * mm});
            skLineSegment(sketch, "E30.4.0", {"start": v(-65.26, -7.62) * mm, "end": v(-65.26, 7.62) * mm});
            skLineSegment(sketch, "E30.4.1", {"start": v(-65.26, 7.62) * mm, "end": v(-62.45, 5.65) * mm});
            skLineSegment(sketch, "E30.4.2", {"start": v(-62.45, 5.65) * mm, "end": v(-62.45, -5.65) * mm});
            skLineSegment(sketch, "E30.4.3", {"start": v(-62.45, -5.65) * mm, "end": v(-65.26, -7.62) * mm});
            skLineSegment(sketch, "E30.5.0", {"start": v(-57.38, -32.01) * mm, "end": v(-63.2, -17.93) * mm});
            skLineSegment(sketch, "E30.5.1", {"start": v(-63.2, -17.93) * mm, "end": v(-59.86, -18.68) * mm});
            skLineSegment(sketch, "E30.5.2", {"start": v(-59.86, -18.68) * mm, "end": v(-55.53, -29.12) * mm});
            skLineSegment(sketch, "E30.5.3", {"start": v(-55.53, -29.12) * mm, "end": v(-57.38, -32.01) * mm});
            skLineSegment(sketch, "E30.6.0", {"start": v(-40.76, -51.53) * mm, "end": v(-51.53, -40.76) * mm});
            skLineSegment(sketch, "E30.6.1", {"start": v(-51.53, -40.76) * mm, "end": v(-48.16, -40.16) * mm});
            skLineSegment(sketch, "E30.6.2", {"start": v(-48.16, -40.16) * mm, "end": v(-40.16, -48.16) * mm});
            skLineSegment(sketch, "E30.6.3", {"start": v(-40.16, -48.16) * mm, "end": v(-40.76, -51.53) * mm});
            skLineSegment(sketch, "E30.7.0", {"start": v(-17.93, -63.2) * mm, "end": v(-32.01, -57.38) * mm});
            skLineSegment(sketch, "E30.7.1", {"start": v(-32.01, -57.38) * mm, "end": v(-29.12, -55.53) * mm});
            skLineSegment(sketch, "E30.7.2", {"start": v(-29.12, -55.53) * mm, "end": v(-18.68, -59.86) * mm});
            skLineSegment(sketch, "E30.7.3", {"start": v(-18.68, -59.86) * mm, "end": v(-17.93, -63.2) * mm});
            skLineSegment(sketch, "E30.8.0", {"start": v(7.62, -65.26) * mm, "end": v(-7.62, -65.26) * mm});
            skLineSegment(sketch, "E30.8.1", {"start": v(-7.62, -65.26) * mm, "end": v(-5.65, -62.45) * mm});
            skLineSegment(sketch, "E30.8.2", {"start": v(-5.65, -62.45) * mm, "end": v(5.65, -62.45) * mm});
            skLineSegment(sketch, "E30.8.3", {"start": v(5.65, -62.45) * mm, "end": v(7.62, -65.26) * mm});
            skLineSegment(sketch, "E30.9.0", {"start": v(32.01, -57.38) * mm, "end": v(17.93, -63.2) * mm});
            skLineSegment(sketch, "E30.9.1", {"start": v(17.93, -63.2) * mm, "end": v(18.68, -59.86) * mm});
            skLineSegment(sketch, "E30.9.2", {"start": v(18.68, -59.86) * mm, "end": v(29.12, -55.53) * mm});
            skLineSegment(sketch, "E30.9.3", {"start": v(29.12, -55.53) * mm, "end": v(32.01, -57.38) * mm});
            skLineSegment(sketch, "E30.10.0", {"start": v(51.53, -40.76) * mm, "end": v(40.76, -51.53) * mm});
            skLineSegment(sketch, "E30.10.1", {"start": v(40.76, -51.53) * mm, "end": v(40.16, -48.16) * mm});
            skLineSegment(sketch, "E30.10.2", {"start": v(40.16, -48.16) * mm, "end": v(48.16, -40.16) * mm});
            skLineSegment(sketch, "E30.10.3", {"start": v(48.16, -40.16) * mm, "end": v(51.53, -40.76) * mm});
            skLineSegment(sketch, "E30.11.0", {"start": v(63.2, -17.93) * mm, "end": v(57.38, -32.01) * mm});
            skLineSegment(sketch, "E30.11.1", {"start": v(57.38, -32.01) * mm, "end": v(55.53, -29.12) * mm});
            skLineSegment(sketch, "E30.11.2", {"start": v(55.53, -29.12) * mm, "end": v(59.86, -18.68) * mm});
            skLineSegment(sketch, "E30.11.3", {"start": v(59.86, -18.68) * mm, "end": v(63.2, -17.93) * mm});
            skLineSegment(sketch, "E30.12.0", {"start": v(65.26, 7.62) * mm, "end": v(65.26, -7.62) * mm});
            skLineSegment(sketch, "E30.12.1", {"start": v(65.26, -7.62) * mm, "end": v(62.45, -5.65) * mm});
            skLineSegment(sketch, "E30.12.2", {"start": v(62.45, -5.65) * mm, "end": v(62.45, 5.65) * mm});
            skLineSegment(sketch, "E30.12.3", {"start": v(62.45, 5.65) * mm, "end": v(65.26, 7.62) * mm});
            skLineSegment(sketch, "E30.13.0", {"start": v(57.38, 32.01) * mm, "end": v(63.2, 17.93) * mm});
            skLineSegment(sketch, "E30.13.1", {"start": v(63.2, 17.93) * mm, "end": v(59.86, 18.68) * mm});
            skLineSegment(sketch, "E30.13.2", {"start": v(59.86, 18.68) * mm, "end": v(55.53, 29.12) * mm});
            skLineSegment(sketch, "E30.13.3", {"start": v(55.53, 29.12) * mm, "end": v(57.38, 32.01) * mm});
            skLineSegment(sketch, "E30.14.0", {"start": v(40.76, 51.53) * mm, "end": v(51.53, 40.76) * mm});
            skLineSegment(sketch, "E30.14.1", {"start": v(51.53, 40.76) * mm, "end": v(48.16, 40.16) * mm});
            skLineSegment(sketch, "E30.14.2", {"start": v(48.16, 40.16) * mm, "end": v(40.16, 48.16) * mm});
            skLineSegment(sketch, "E30.14.3", {"start": v(40.16, 48.16) * mm, "end": v(40.76, 51.53) * mm});
            skLineSegment(sketch, "E30.15.0", {"start": v(17.93, 63.2) * mm, "end": v(32.01, 57.38) * mm});
            skLineSegment(sketch, "E30.15.1", {"start": v(32.01, 57.38) * mm, "end": v(29.12, 55.53) * mm});
            skLineSegment(sketch, "E30.15.2", {"start": v(29.12, 55.53) * mm, "end": v(18.68, 59.86) * mm});
            skLineSegment(sketch, "E30.15.3", {"start": v(18.68, 59.86) * mm, "end": v(17.93, 63.2) * mm});
            skPoint(sketch, "E30.center", {"position": v(0, 0) * mm});
            skSolve(sketch);
        }
        {
            var Q0;
            Q0 = qSketchRegion(id + "F12", true);
            extrude(context, id + "F13", {"entities" : qUnion([Q0]), "operationType" : NewBodyOperationType.REMOVE, "oppositeDirection" : true, "depth" : 1.02 * mm});
        }
    });
